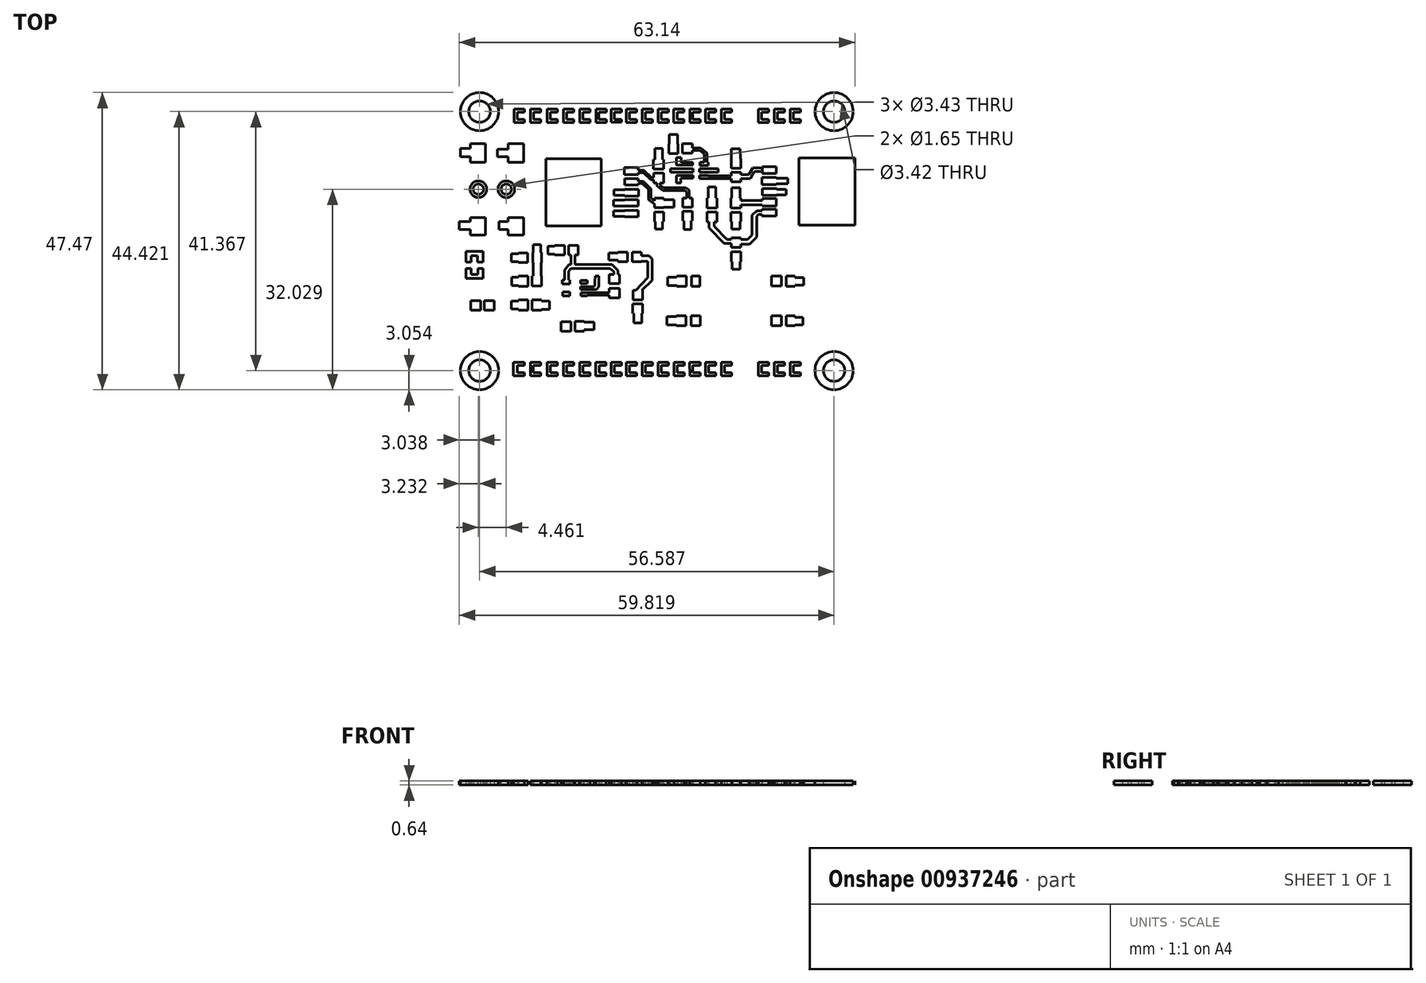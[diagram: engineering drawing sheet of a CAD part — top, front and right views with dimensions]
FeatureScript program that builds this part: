
annotation { "Feature Type Name" : "Feature", "Feature Type Description" : "" }
export const myFeature = defineFeature(function(context is Context, id is Id, definition is map)
    precondition{}
    {
        {
            var Q0;
            Q0=qCreatedBy(makeId("Top.planeOp"),FACE);
            var sketch = newSketch(context, id + "F0", { "sketchPlane" : qUnion([Q0])});
            skLineSegment(sketch, "E0.bottom", {"start": v(-31.07, 17.75) * mm, "end": v(37.51, 17.75) * mm});
            skLineSegment(sketch, "E0.top", {"start": v(-31.07, -35.59) * mm, "end": v(37.51, -35.59) * mm});
            skLineSegment(sketch, "E0.left", {"start": v(-31.07, 17.75) * mm, "end": v(-31.07, -35.59) * mm});
            skLineSegment(sketch, "E0.right", {"start": v(37.51, 17.75) * mm, "end": v(37.51, -35.59) * mm});
            skLineSegment(sketch, "E1.bottom", {"start": v(-26.63, 6.76) * mm, "end": v(-24.16, 6.76) * mm});
            skLineSegment(sketch, "E1.top", {"start": v(-26.63, 3.78) * mm, "end": v(-24.16, 3.78) * mm});
            skLineSegment(sketch, "E1.left", {"start": v(-26.63, 6.76) * mm, "end": v(-26.63, 3.78) * mm});
            skLineSegment(sketch, "E1.right", {"start": v(-24.16, 6.76) * mm, "end": v(-24.16, 3.78) * mm});
            skLineSegment(sketch, "E2.bottom", {"start": v(-20.57, 6.76) * mm, "end": v(-18.08, 6.76) * mm});
            skLineSegment(sketch, "E2.top", {"start": v(-20.57, 3.78) * mm, "end": v(-18.08, 3.78) * mm});
            skLineSegment(sketch, "E2.left", {"start": v(-20.57, 6.76) * mm, "end": v(-20.57, 3.78) * mm});
            skLineSegment(sketch, "E2.right", {"start": v(-18.08, 6.76) * mm, "end": v(-18.08, 3.78) * mm});
            skLineSegment(sketch, "E3.bottom", {"start": v(-26.63, -5.07) * mm, "end": v(-24.16, -5.07) * mm});
            skLineSegment(sketch, "E3.top", {"start": v(-26.63, -7.89) * mm, "end": v(-24.16, -7.89) * mm});
            skLineSegment(sketch, "E3.left", {"start": v(-26.63, -5.07) * mm, "end": v(-26.63, -7.89) * mm});
            skLineSegment(sketch, "E3.right", {"start": v(-24.16, -5.07) * mm, "end": v(-24.16, -7.89) * mm});
            skLineSegment(sketch, "E4.bottom", {"start": v(-20.57, -5.05) * mm, "end": v(-18.1, -5.05) * mm});
            skLineSegment(sketch, "E4.top", {"start": v(-20.57, -7.89) * mm, "end": v(-18.1, -7.89) * mm});
            skLineSegment(sketch, "E4.left", {"start": v(-20.57, -5.05) * mm, "end": v(-20.57, -7.89) * mm});
            skLineSegment(sketch, "E4.right", {"start": v(-18.1, -5.05) * mm, "end": v(-18.1, -7.89) * mm});
            skLineSegment(sketch, "E5.bottom", {"start": v(-26.53, -18.31) * mm, "end": v(-24.97, -18.31) * mm});
            skLineSegment(sketch, "E5.top", {"start": v(-26.53, -19.88) * mm, "end": v(-24.97, -19.88) * mm});
            skLineSegment(sketch, "E5.left", {"start": v(-26.53, -18.31) * mm, "end": v(-26.53, -19.88) * mm});
            skLineSegment(sketch, "E5.right", {"start": v(-24.97, -18.31) * mm, "end": v(-24.97, -19.88) * mm});
            skLineSegment(sketch, "E6.bottom", {"start": v(-24.36, -18.31) * mm, "end": v(-22.8, -18.31) * mm});
            skLineSegment(sketch, "E6.top", {"start": v(-24.36, -19.88) * mm, "end": v(-22.8, -19.88) * mm});
            skLineSegment(sketch, "E6.left", {"start": v(-24.36, -18.31) * mm, "end": v(-24.36, -19.88) * mm});
            skLineSegment(sketch, "E6.right", {"start": v(-22.8, -18.31) * mm, "end": v(-22.8, -19.88) * mm});
            skLineSegment(sketch, "E7.bottom", {"start": v(-18.92, -18.23) * mm, "end": v(-17.4, -18.23) * mm});
            skLineSegment(sketch, "E7.top", {"start": v(-18.92, -19.88) * mm, "end": v(-17.4, -19.88) * mm});
            skLineSegment(sketch, "E7.left", {"start": v(-18.92, -18.23) * mm, "end": v(-18.92, -19.88) * mm});
            skLineSegment(sketch, "E7.right", {"start": v(-17.4, -18.23) * mm, "end": v(-17.4, -19.88) * mm});
            skLineSegment(sketch, "E8.bottom", {"start": v(-16.76, -18.22) * mm, "end": v(-15.23, -18.22) * mm});
            skLineSegment(sketch, "E8.top", {"start": v(-16.76, -19.88) * mm, "end": v(-15.23, -19.88) * mm});
            skLineSegment(sketch, "E8.left", {"start": v(-16.76, -18.22) * mm, "end": v(-16.76, -19.88) * mm});
            skLineSegment(sketch, "E8.right", {"start": v(-15.23, -18.22) * mm, "end": v(-15.23, -19.88) * mm});
            skLineSegment(sketch, "E9.bottom", {"start": v(-18.95, -14.37) * mm, "end": v(-17.42, -14.37) * mm});
            skLineSegment(sketch, "E9.top", {"start": v(-18.95, -16.02) * mm, "end": v(-17.42, -16.02) * mm});
            skLineSegment(sketch, "E9.left", {"start": v(-18.95, -14.37) * mm, "end": v(-18.95, -16.02) * mm});
            skLineSegment(sketch, "E9.right", {"start": v(-17.42, -14.37) * mm, "end": v(-17.42, -16.02) * mm});
            skLineSegment(sketch, "E10.bottom", {"start": v(-16.76, -14.4) * mm, "end": v(-15.22, -14.4) * mm});
            skLineSegment(sketch, "E10.top", {"start": v(-16.76, -15.97) * mm, "end": v(-15.22, -15.97) * mm});
            skLineSegment(sketch, "E10.left", {"start": v(-16.76, -14.4) * mm, "end": v(-16.76, -15.97) * mm});
            skLineSegment(sketch, "E10.right", {"start": v(-15.22, -14.4) * mm, "end": v(-15.22, -15.97) * mm});
            skLineSegment(sketch, "E11.bottom", {"start": v(-18.92, -10.7) * mm, "end": v(-17.45, -10.7) * mm});
            skLineSegment(sketch, "E11.top", {"start": v(-18.92, -12.22) * mm, "end": v(-17.45, -12.22) * mm});
            skLineSegment(sketch, "E11.left", {"start": v(-18.92, -10.7) * mm, "end": v(-18.92, -12.22) * mm});
            skLineSegment(sketch, "E11.right", {"start": v(-17.45, -10.7) * mm, "end": v(-17.45, -12.22) * mm});
            skLineSegment(sketch, "E12.bottom", {"start": v(-16.66, -10.66) * mm, "end": v(-15.22, -10.66) * mm});
            skLineSegment(sketch, "E12.top", {"start": v(-16.66, -12.26) * mm, "end": v(-15.22, -12.26) * mm});
            skLineSegment(sketch, "E12.left", {"start": v(-16.66, -10.66) * mm, "end": v(-16.66, -12.26) * mm});
            skLineSegment(sketch, "E12.right", {"start": v(-15.22, -10.66) * mm, "end": v(-15.22, -12.26) * mm});
            skLineSegment(sketch, "E13.bottom", {"start": v(-13.14, -9.5) * mm, "end": v(-11.55, -9.5) * mm});
            skLineSegment(sketch, "E13.top", {"start": v(-13.14, -11.04) * mm, "end": v(-11.55, -11.04) * mm});
            skLineSegment(sketch, "E13.left", {"start": v(-13.14, -9.5) * mm, "end": v(-13.14, -11.04) * mm});
            skLineSegment(sketch, "E13.right", {"start": v(-11.55, -9.5) * mm, "end": v(-11.55, -11.04) * mm});
            skLineSegment(sketch, "E14.bottom", {"start": v(-10.92, -9.52) * mm, "end": v(-9.4, -9.52) * mm});
            skLineSegment(sketch, "E14.top", {"start": v(-10.92, -11.03) * mm, "end": v(-9.4, -11.03) * mm});
            skLineSegment(sketch, "E14.left", {"start": v(-10.92, -9.52) * mm, "end": v(-10.92, -11.03) * mm});
            skLineSegment(sketch, "E14.right", {"start": v(-9.4, -9.52) * mm, "end": v(-9.4, -11.03) * mm});
            skLineSegment(sketch, "E15.bottom", {"start": v(-11.94, -15.04) * mm, "end": v(-10.75, -15.04) * mm});
            skLineSegment(sketch, "E15.top", {"start": v(-11.94, -15.65) * mm, "end": v(-10.75, -15.65) * mm});
            skLineSegment(sketch, "E15.left", {"start": v(-11.94, -15.04) * mm, "end": v(-11.94, -15.65) * mm});
            skLineSegment(sketch, "E15.right", {"start": v(-10.75, -15.04) * mm, "end": v(-10.75, -15.65) * mm});
            skLineSegment(sketch, "E16.bottom", {"start": v(-9.02, -15.07) * mm, "end": v(-7.94, -15.07) * mm});
            skLineSegment(sketch, "E16.top", {"start": v(-9.02, -15.58) * mm, "end": v(-7.94, -15.58) * mm});
            skLineSegment(sketch, "E16.left", {"start": v(-9.02, -15.07) * mm, "end": v(-9.02, -15.58) * mm});
            skLineSegment(sketch, "E16.right", {"start": v(-7.94, -15.07) * mm, "end": v(-7.94, -15.58) * mm});
            skLineSegment(sketch, "E17.bottom", {"start": v(-9.02, -16.11) * mm, "end": v(-7.94, -16.11) * mm});
            skLineSegment(sketch, "E17.top", {"start": v(-9.02, -16.57) * mm, "end": v(-7.94, -16.57) * mm});
            skLineSegment(sketch, "E17.left", {"start": v(-9.02, -16.11) * mm, "end": v(-9.02, -16.57) * mm});
            skLineSegment(sketch, "E17.right", {"start": v(-7.94, -16.11) * mm, "end": v(-7.94, -16.57) * mm});
            skLineSegment(sketch, "E18.bottom", {"start": v(-8.98, -17.09) * mm, "end": v(-7.92, -17.09) * mm});
            skLineSegment(sketch, "E18.top", {"start": v(-8.98, -17.56) * mm, "end": v(-7.92, -17.56) * mm});
            skLineSegment(sketch, "E18.left", {"start": v(-8.98, -17.09) * mm, "end": v(-8.98, -17.56) * mm});
            skLineSegment(sketch, "E18.right", {"start": v(-7.92, -17.09) * mm, "end": v(-7.92, -17.56) * mm});
            skLineSegment(sketch, "E19.bottom", {"start": v(-11.85, -16.92) * mm, "end": v(-10.75, -16.92) * mm});
            skLineSegment(sketch, "E19.top", {"start": v(-11.85, -17.55) * mm, "end": v(-10.75, -17.55) * mm});
            skLineSegment(sketch, "E19.left", {"start": v(-11.85, -16.92) * mm, "end": v(-11.85, -17.55) * mm});
            skLineSegment(sketch, "E19.right", {"start": v(-10.75, -16.92) * mm, "end": v(-10.75, -17.55) * mm});
            skLineSegment(sketch, "E20.bottom", {"start": v(-4.44, -14.17) * mm, "end": v(-2.8, -14.17) * mm});
            skLineSegment(sketch, "E20.top", {"start": v(-4.44, -15.62) * mm, "end": v(-2.8, -15.62) * mm});
            skLineSegment(sketch, "E20.left", {"start": v(-4.44, -14.17) * mm, "end": v(-4.44, -15.62) * mm});
            skLineSegment(sketch, "E20.right", {"start": v(-2.8, -14.17) * mm, "end": v(-2.8, -15.62) * mm});
            skLineSegment(sketch, "E21.bottom", {"start": v(-4.43, -16.34) * mm, "end": v(-2.81, -16.34) * mm});
            skLineSegment(sketch, "E21.top", {"start": v(-4.43, -17.87) * mm, "end": v(-2.81, -17.87) * mm});
            skLineSegment(sketch, "E21.left", {"start": v(-4.43, -16.34) * mm, "end": v(-4.43, -17.87) * mm});
            skLineSegment(sketch, "E21.right", {"start": v(-2.81, -16.34) * mm, "end": v(-2.81, -17.87) * mm});
            skLineSegment(sketch, "E22.bottom", {"start": v(-12.1, -21.7) * mm, "end": v(-10.55, -21.7) * mm});
            skLineSegment(sketch, "E22.top", {"start": v(-12.1, -23.23) * mm, "end": v(-10.55, -23.23) * mm});
            skLineSegment(sketch, "E22.left", {"start": v(-12.1, -21.7) * mm, "end": v(-12.1, -23.23) * mm});
            skLineSegment(sketch, "E22.right", {"start": v(-10.55, -21.7) * mm, "end": v(-10.55, -23.23) * mm});
            skLineSegment(sketch, "E23.bottom", {"start": v(-9.93, -21.66) * mm, "end": v(-8.43, -21.66) * mm});
            skLineSegment(sketch, "E23.top", {"start": v(-9.93, -23.22) * mm, "end": v(-8.43, -23.22) * mm});
            skLineSegment(sketch, "E23.left", {"start": v(-9.93, -21.66) * mm, "end": v(-9.93, -23.22) * mm});
            skLineSegment(sketch, "E23.right", {"start": v(-8.43, -21.66) * mm, "end": v(-8.43, -23.22) * mm});
            skLineSegment(sketch, "E24.bottom", {"start": v(-0.66, -16.68) * mm, "end": v(0.91, -16.68) * mm});
            skLineSegment(sketch, "E24.top", {"start": v(-0.66, -18.23) * mm, "end": v(0.91, -18.23) * mm});
            skLineSegment(sketch, "E24.left", {"start": v(-0.66, -16.68) * mm, "end": v(-0.66, -18.23) * mm});
            skLineSegment(sketch, "E24.right", {"start": v(0.91, -16.68) * mm, "end": v(0.91, -18.23) * mm});
            skLineSegment(sketch, "E25.bottom", {"start": v(-0.68, -18.86) * mm, "end": v(0.91, -18.86) * mm});
            skLineSegment(sketch, "E25.top", {"start": v(-0.68, -20.36) * mm, "end": v(0.91, -20.36) * mm});
            skLineSegment(sketch, "E25.left", {"start": v(-0.68, -18.86) * mm, "end": v(-0.68, -20.36) * mm});
            skLineSegment(sketch, "E25.right", {"start": v(0.91, -18.86) * mm, "end": v(0.91, -20.36) * mm});
            skLineSegment(sketch, "E26.bottom", {"start": v(-3.03, -10.56) * mm, "end": v(-1.5, -10.56) * mm});
            skLineSegment(sketch, "E26.top", {"start": v(-3.03, -12.08) * mm, "end": v(-1.5, -12.08) * mm});
            skLineSegment(sketch, "E26.left", {"start": v(-3.03, -10.56) * mm, "end": v(-3.03, -12.08) * mm});
            skLineSegment(sketch, "E26.right", {"start": v(-1.5, -10.56) * mm, "end": v(-1.5, -12.08) * mm});
            skLineSegment(sketch, "E27.bottom", {"start": v(-0.78, -10.56) * mm, "end": v(0.7, -10.56) * mm});
            skLineSegment(sketch, "E27.top", {"start": v(-0.78, -12.1) * mm, "end": v(0.7, -12.1) * mm});
            skLineSegment(sketch, "E27.left", {"start": v(-0.78, -10.56) * mm, "end": v(-0.78, -12.1) * mm});
            skLineSegment(sketch, "E27.right", {"start": v(0.7, -10.56) * mm, "end": v(0.7, -12.1) * mm});
            skLineSegment(sketch, "E28.bottom", {"start": v(6.35, -14.4) * mm, "end": v(7.85, -14.4) * mm});
            skLineSegment(sketch, "E28.top", {"start": v(6.35, -16.02) * mm, "end": v(7.85, -16.02) * mm});
            skLineSegment(sketch, "E28.left", {"start": v(6.35, -14.4) * mm, "end": v(6.35, -16.02) * mm});
            skLineSegment(sketch, "E28.right", {"start": v(7.85, -14.4) * mm, "end": v(7.85, -16.02) * mm});
            skLineSegment(sketch, "E29.bottom", {"start": v(8.67, -14.4) * mm, "end": v(10.04, -14.4) * mm});
            skLineSegment(sketch, "E29.top", {"start": v(8.67, -16.04) * mm, "end": v(10.04, -16.04) * mm});
            skLineSegment(sketch, "E29.left", {"start": v(8.67, -14.4) * mm, "end": v(8.67, -16.04) * mm});
            skLineSegment(sketch, "E29.right", {"start": v(10.04, -14.4) * mm, "end": v(10.04, -16.04) * mm});
            skLineSegment(sketch, "E30.bottom", {"start": v(6.3, -20.72) * mm, "end": v(7.84, -20.72) * mm});
            skLineSegment(sketch, "E30.top", {"start": v(6.3, -22.36) * mm, "end": v(7.84, -22.36) * mm});
            skLineSegment(sketch, "E30.left", {"start": v(6.3, -20.72) * mm, "end": v(6.3, -22.36) * mm});
            skLineSegment(sketch, "E30.right", {"start": v(7.84, -20.72) * mm, "end": v(7.84, -22.36) * mm});
            skLineSegment(sketch, "E31.bottom", {"start": v(8.65, -20.75) * mm, "end": v(10.09, -20.75) * mm});
            skLineSegment(sketch, "E31.top", {"start": v(8.65, -22.33) * mm, "end": v(10.09, -22.33) * mm});
            skLineSegment(sketch, "E31.left", {"start": v(8.65, -20.75) * mm, "end": v(8.65, -22.33) * mm});
            skLineSegment(sketch, "E31.right", {"start": v(10.09, -20.75) * mm, "end": v(10.09, -22.33) * mm});
            skLineSegment(sketch, "E32.bottom", {"start": v(21.47, -20.74) * mm, "end": v(23.04, -20.74) * mm});
            skLineSegment(sketch, "E32.top", {"start": v(21.47, -22.34) * mm, "end": v(23.04, -22.34) * mm});
            skLineSegment(sketch, "E32.left", {"start": v(21.47, -20.74) * mm, "end": v(21.47, -22.34) * mm});
            skLineSegment(sketch, "E32.right", {"start": v(23.04, -20.74) * mm, "end": v(23.04, -22.34) * mm});
            skLineSegment(sketch, "E33.bottom", {"start": v(23.84, -20.72) * mm, "end": v(25.2, -20.72) * mm});
            skLineSegment(sketch, "E33.top", {"start": v(23.84, -22.35) * mm, "end": v(25.2, -22.35) * mm});
            skLineSegment(sketch, "E33.left", {"start": v(23.84, -20.72) * mm, "end": v(23.84, -22.35) * mm});
            skLineSegment(sketch, "E33.right", {"start": v(25.2, -20.72) * mm, "end": v(25.2, -22.35) * mm});
            skLineSegment(sketch, "E34.bottom", {"start": v(21.5, -14.4) * mm, "end": v(23.04, -14.4) * mm});
            skLineSegment(sketch, "E34.top", {"start": v(21.5, -16.01) * mm, "end": v(23.04, -16.01) * mm});
            skLineSegment(sketch, "E34.left", {"start": v(21.5, -14.4) * mm, "end": v(21.5, -16.01) * mm});
            skLineSegment(sketch, "E34.right", {"start": v(23.04, -14.4) * mm, "end": v(23.04, -16.01) * mm});
            skLineSegment(sketch, "E35.bottom", {"start": v(23.82, -14.4) * mm, "end": v(25.2, -14.4) * mm});
            skLineSegment(sketch, "E35.top", {"start": v(23.82, -16.05) * mm, "end": v(25.2, -16.05) * mm});
            skLineSegment(sketch, "E35.left", {"start": v(23.82, -14.4) * mm, "end": v(23.82, -16.05) * mm});
            skLineSegment(sketch, "E35.right", {"start": v(25.2, -14.4) * mm, "end": v(25.2, -16.05) * mm});
            skLineSegment(sketch, "E36.bottom", {"start": v(15.02, -8.31) * mm, "end": v(16.56, -8.31) * mm});
            skLineSegment(sketch, "E36.top", {"start": v(15.02, -9.8) * mm, "end": v(16.56, -9.8) * mm});
            skLineSegment(sketch, "E36.left", {"start": v(15.02, -8.31) * mm, "end": v(15.02, -9.8) * mm});
            skLineSegment(sketch, "E36.right", {"start": v(16.56, -8.31) * mm, "end": v(16.56, -9.8) * mm});
            skLineSegment(sketch, "E37.bottom", {"start": v(15.02, -10.53) * mm, "end": v(16.56, -10.53) * mm});
            skLineSegment(sketch, "E37.top", {"start": v(15.02, -12.1) * mm, "end": v(16.56, -12.1) * mm});
            skLineSegment(sketch, "E37.left", {"start": v(15.02, -10.53) * mm, "end": v(15.02, -12.1) * mm});
            skLineSegment(sketch, "E37.right", {"start": v(16.56, -10.53) * mm, "end": v(16.56, -12.1) * mm});
            skLineSegment(sketch, "E38.bottom", {"start": v(-14.57, 4.35) * mm, "end": v(-5.73, 4.35) * mm});
            skLineSegment(sketch, "E38.top", {"start": v(-14.57, -6.38) * mm, "end": v(-5.73, -6.38) * mm});
            skLineSegment(sketch, "E38.left", {"start": v(-14.57, 4.35) * mm, "end": v(-14.57, -6.38) * mm});
            skLineSegment(sketch, "E38.right", {"start": v(-5.73, 4.35) * mm, "end": v(-5.73, -6.38) * mm});
            skLineSegment(sketch, "E39.bottom", {"start": v(-2.05, 2.91) * mm, "end": v(0.22, 2.91) * mm});
            skLineSegment(sketch, "E39.top", {"start": v(-2.05, 1.8) * mm, "end": v(0.22, 1.8) * mm});
            skLineSegment(sketch, "E39.left", {"start": v(-2.05, 2.91) * mm, "end": v(-2.05, 1.8) * mm});
            skLineSegment(sketch, "E39.right", {"start": v(0.22, 2.91) * mm, "end": v(0.22, 1.8) * mm});
            skLineSegment(sketch, "E40.bottom", {"start": v(-1.99, 1.18) * mm, "end": v(0.2, 1.18) * mm});
            skLineSegment(sketch, "E40.top", {"start": v(-1.99, 0.15) * mm, "end": v(0.2, 0.15) * mm});
            skLineSegment(sketch, "E40.left", {"start": v(-1.99, 1.18) * mm, "end": v(-1.99, 0.15) * mm});
            skLineSegment(sketch, "E41.bottom", {"start": v(-1.96, -0.53) * mm, "end": v(0.24, -0.53) * mm});
            skLineSegment(sketch, "E41.top", {"start": v(-1.96, -1.6) * mm, "end": v(0.24, -1.6) * mm});
            skLineSegment(sketch, "E41.left", {"start": v(-1.96, -0.53) * mm, "end": v(-1.96, -1.6) * mm});
            skLineSegment(sketch, "E41.right", {"start": v(0.24, -0.53) * mm, "end": v(0.24, -1.6) * mm});
            skLineSegment(sketch, "E42.bottom", {"start": v(-1.96, -2.2) * mm, "end": v(0.2, -2.2) * mm});
            skLineSegment(sketch, "E42.top", {"start": v(-1.96, -3.25) * mm, "end": v(0.2, -3.25) * mm});
            skLineSegment(sketch, "E42.left", {"start": v(-1.96, -2.2) * mm, "end": v(-1.96, -3.25) * mm});
            skLineSegment(sketch, "E42.right", {"start": v(0.2, -2.2) * mm, "end": v(0.2, -3.25) * mm});
            skLineSegment(sketch, "E43.bottom", {"start": v(-1.94, -3.92) * mm, "end": v(0.2, -3.92) * mm});
            skLineSegment(sketch, "E43.top", {"start": v(-1.94, -4.94) * mm, "end": v(0.2, -4.94) * mm});
            skLineSegment(sketch, "E43.left", {"start": v(-1.94, -3.92) * mm, "end": v(-1.94, -4.94) * mm});
            skLineSegment(sketch, "E43.right", {"start": v(0.2, -3.92) * mm, "end": v(0.2, -4.94) * mm});
            skLineSegment(sketch, "E44.bottom", {"start": v(2.78, -1.98) * mm, "end": v(4.26, -1.98) * mm});
            skLineSegment(sketch, "E44.top", {"start": v(2.78, -3.48) * mm, "end": v(4.26, -3.48) * mm});
            skLineSegment(sketch, "E45.bottom", {"start": v(2.78, -4.17) * mm, "end": v(4.26, -4.17) * mm});
            skLineSegment(sketch, "E45.top", {"start": v(2.78, -5.72) * mm, "end": v(4.26, -5.72) * mm});
            skLineSegment(sketch, "E45.left", {"start": v(2.78, -4.17) * mm, "end": v(2.78, -5.72) * mm});
            skLineSegment(sketch, "E45.right", {"start": v(4.26, -4.17) * mm, "end": v(4.26, -5.72) * mm});
            skLineSegment(sketch, "E46.bottom", {"start": v(7.3, -1.98) * mm, "end": v(8.83, -1.98) * mm});
            skLineSegment(sketch, "E46.top", {"start": v(7.3, -3.38) * mm, "end": v(8.83, -3.38) * mm});
            skLineSegment(sketch, "E46.left", {"start": v(7.3, -1.98) * mm, "end": v(7.3, -3.38) * mm});
            skLineSegment(sketch, "E46.right", {"start": v(8.83, -1.98) * mm, "end": v(8.83, -3.38) * mm});
            skLineSegment(sketch, "E47.bottom", {"start": v(7.33, -4.04) * mm, "end": v(8.8, -4.04) * mm});
            skLineSegment(sketch, "E47.top", {"start": v(7.33, -5.56) * mm, "end": v(8.8, -5.56) * mm});
            skLineSegment(sketch, "E47.left", {"start": v(7.33, -4.04) * mm, "end": v(7.33, -5.56) * mm});
            skLineSegment(sketch, "E47.right", {"start": v(8.8, -4.04) * mm, "end": v(8.8, -5.56) * mm});
            skLineSegment(sketch, "E48.bottom", {"start": v(11.2, -1.98) * mm, "end": v(12.75, -1.98) * mm});
            skLineSegment(sketch, "E48.top", {"start": v(11.2, -3.53) * mm, "end": v(12.75, -3.53) * mm});
            skLineSegment(sketch, "E48.left", {"start": v(11.2, -1.98) * mm, "end": v(11.2, -3.53) * mm});
            skLineSegment(sketch, "E48.right", {"start": v(12.75, -1.98) * mm, "end": v(12.75, -3.53) * mm});
            skLineSegment(sketch, "E49.bottom", {"start": v(11.18, -4.2) * mm, "end": v(12.8, -4.2) * mm});
            skLineSegment(sketch, "E49.top", {"start": v(11.18, -5.74) * mm, "end": v(12.8, -5.74) * mm});
            skLineSegment(sketch, "E49.left", {"start": v(11.18, -4.2) * mm, "end": v(11.18, -5.74) * mm});
            skLineSegment(sketch, "E49.right", {"start": v(12.8, -4.2) * mm, "end": v(12.8, -5.74) * mm});
            skLineSegment(sketch, "E50.bottom", {"start": v(15, -1.98) * mm, "end": v(16.56, -1.98) * mm});
            skLineSegment(sketch, "E50.top", {"start": v(15, -3.53) * mm, "end": v(16.56, -3.53) * mm});
            skLineSegment(sketch, "E50.left", {"start": v(15, -1.98) * mm, "end": v(15, -3.53) * mm});
            skLineSegment(sketch, "E50.right", {"start": v(16.56, -1.98) * mm, "end": v(16.56, -3.53) * mm});
            skLineSegment(sketch, "E51.bottom", {"start": v(15, -4.21) * mm, "end": v(16.56, -4.21) * mm});
            skLineSegment(sketch, "E51.top", {"start": v(15, -5.7) * mm, "end": v(16.56, -5.7) * mm});
            skLineSegment(sketch, "E51.left", {"start": v(15, -4.21) * mm, "end": v(15, -5.7) * mm});
            skLineSegment(sketch, "E51.right", {"start": v(16.56, -4.21) * mm, "end": v(16.56, -5.7) * mm});
            skLineSegment(sketch, "E52.bottom", {"start": v(2.63, 4.23) * mm, "end": v(4.26, 4.23) * mm});
            skLineSegment(sketch, "E52.top", {"start": v(2.63, 2.69) * mm, "end": v(4.26, 2.69) * mm});
            skLineSegment(sketch, "E52.left", {"start": v(2.63, 4.23) * mm, "end": v(2.63, 2.69) * mm});
            skLineSegment(sketch, "E52.right", {"start": v(4.26, 4.23) * mm, "end": v(4.26, 2.69) * mm});
            skLineSegment(sketch, "E53.bottom", {"start": v(2.69, 2.05) * mm, "end": v(4.26, 2.05) * mm});
            skLineSegment(sketch, "E53.top", {"start": v(2.69, 0.47) * mm, "end": v(4.26, 0.47) * mm});
            skLineSegment(sketch, "E53.left", {"start": v(2.69, 2.05) * mm, "end": v(2.69, 0.47) * mm});
            skLineSegment(sketch, "E53.right", {"start": v(4.26, 2.05) * mm, "end": v(4.26, 0.47) * mm});
            skLineSegment(sketch, "E54.bottom", {"start": v(5.07, 6.7) * mm, "end": v(6.56, 6.7) * mm});
            skLineSegment(sketch, "E54.top", {"start": v(5.07, 5.16) * mm, "end": v(6.56, 5.16) * mm});
            skLineSegment(sketch, "E54.left", {"start": v(5.07, 6.7) * mm, "end": v(5.07, 5.16) * mm});
            skLineSegment(sketch, "E54.right", {"start": v(6.56, 6.7) * mm, "end": v(6.56, 5.16) * mm});
            skLineSegment(sketch, "E55.bottom", {"start": v(7.25, 6.75) * mm, "end": v(8.8, 6.75) * mm});
            skLineSegment(sketch, "E55.top", {"start": v(7.25, 5.2) * mm, "end": v(8.8, 5.2) * mm});
            skLineSegment(sketch, "E55.left", {"start": v(7.25, 6.75) * mm, "end": v(7.25, 5.2) * mm});
            skLineSegment(sketch, "E55.right", {"start": v(8.8, 6.75) * mm, "end": v(8.8, 5.2) * mm});
            skLineSegment(sketch, "E56.bottom", {"start": v(7.57, 3.78) * mm, "end": v(8.91, 3.78) * mm});
            skLineSegment(sketch, "E56.top", {"start": v(7.57, 3.34) * mm, "end": v(8.91, 3.34) * mm});
            skLineSegment(sketch, "E56.left", {"start": v(7.57, 3.78) * mm, "end": v(7.57, 3.34) * mm});
            skLineSegment(sketch, "E56.right", {"start": v(8.91, 3.78) * mm, "end": v(8.91, 3.34) * mm});
            skLineSegment(sketch, "E57.bottom", {"start": v(7.65, 2.78) * mm, "end": v(8.93, 2.78) * mm});
            skLineSegment(sketch, "E57.top", {"start": v(7.65, 2.18) * mm, "end": v(8.93, 2.18) * mm});
            skLineSegment(sketch, "E57.left", {"start": v(7.65, 2.78) * mm, "end": v(7.65, 2.18) * mm});
            skLineSegment(sketch, "E57.right", {"start": v(8.93, 2.78) * mm, "end": v(8.93, 2.18) * mm});
            skLineSegment(sketch, "E58.bottom", {"start": v(7.56, 1.64) * mm, "end": v(8.93, 1.64) * mm});
            skLineSegment(sketch, "E58.top", {"start": v(7.56, 1.2) * mm, "end": v(8.93, 1.2) * mm});
            skLineSegment(sketch, "E58.left", {"start": v(7.56, 1.64) * mm, "end": v(7.56, 1.2) * mm});
            skLineSegment(sketch, "E58.right", {"start": v(8.93, 1.64) * mm, "end": v(8.93, 1.2) * mm});
            skLineSegment(sketch, "E59.bottom", {"start": v(10.04, 3.78) * mm, "end": v(11.4, 3.78) * mm});
            skLineSegment(sketch, "E59.top", {"start": v(10.04, 3.28) * mm, "end": v(11.4, 3.28) * mm});
            skLineSegment(sketch, "E59.left", {"start": v(10.04, 3.78) * mm, "end": v(10.04, 3.28) * mm});
            skLineSegment(sketch, "E59.right", {"start": v(11.4, 3.78) * mm, "end": v(11.4, 3.28) * mm});
            skLineSegment(sketch, "E60.bottom", {"start": v(10, 2.76) * mm, "end": v(11.41, 2.76) * mm});
            skLineSegment(sketch, "E60.top", {"start": v(10, 2.2) * mm, "end": v(11.41, 2.2) * mm});
            skLineSegment(sketch, "E60.left", {"start": v(10, 2.76) * mm, "end": v(10, 2.2) * mm});
            skLineSegment(sketch, "E60.right", {"start": v(11.41, 2.76) * mm, "end": v(11.41, 2.2) * mm});
            skLineSegment(sketch, "E61.bottom", {"start": v(10, 1.64) * mm, "end": v(11.38, 1.64) * mm});
            skLineSegment(sketch, "E61.top", {"start": v(10, 1.19) * mm, "end": v(11.38, 1.19) * mm});
            skLineSegment(sketch, "E61.left", {"start": v(10, 1.64) * mm, "end": v(10, 1.19) * mm});
            skLineSegment(sketch, "E61.right", {"start": v(11.38, 1.64) * mm, "end": v(11.38, 1.19) * mm});
            skLineSegment(sketch, "E62.bottom", {"start": v(15.05, 4.36) * mm, "end": v(16.57, 4.36) * mm});
            skLineSegment(sketch, "E62.top", {"start": v(15.05, 2.82) * mm, "end": v(16.57, 2.82) * mm});
            skLineSegment(sketch, "E62.left", {"start": v(15.05, 4.36) * mm, "end": v(15.05, 2.82) * mm});
            skLineSegment(sketch, "E62.right", {"start": v(16.57, 4.36) * mm, "end": v(16.57, 2.82) * mm});
            skLineSegment(sketch, "E63.bottom", {"start": v(15.05, 2.15) * mm, "end": v(16.57, 2.15) * mm});
            skLineSegment(sketch, "E63.top", {"start": v(15.05, 0.63) * mm, "end": v(16.57, 0.63) * mm});
            skLineSegment(sketch, "E63.left", {"start": v(15.05, 2.15) * mm, "end": v(15.05, 0.63) * mm});
            skLineSegment(sketch, "E63.right", {"start": v(16.57, 2.15) * mm, "end": v(16.57, 0.63) * mm});
            skLineSegment(sketch, "E64.bottom", {"start": v(19.98, 3.05) * mm, "end": v(22.23, 3.05) * mm});
            skLineSegment(sketch, "E64.top", {"start": v(19.98, 1.97) * mm, "end": v(22.23, 1.97) * mm});
            skLineSegment(sketch, "E64.left", {"start": v(19.98, 3.05) * mm, "end": v(19.98, 1.97) * mm});
            skLineSegment(sketch, "E64.right", {"start": v(22.23, 3.05) * mm, "end": v(22.23, 1.97) * mm});
            skLineSegment(sketch, "E65.bottom", {"start": v(19.93, 1.34) * mm, "end": v(22.23, 1.34) * mm});
            skLineSegment(sketch, "E65.top", {"start": v(19.93, 0.24) * mm, "end": v(22.23, 0.24) * mm});
            skLineSegment(sketch, "E65.left", {"start": v(19.93, 1.34) * mm, "end": v(19.93, 0.24) * mm});
            skLineSegment(sketch, "E65.right", {"start": v(22.23, 1.34) * mm, "end": v(22.23, 0.24) * mm});
            skLineSegment(sketch, "E66.bottom", {"start": v(19.98, -0.45) * mm, "end": v(22.27, -0.45) * mm});
            skLineSegment(sketch, "E66.top", {"start": v(19.98, -1.5) * mm, "end": v(22.27, -1.5) * mm});
            skLineSegment(sketch, "E66.left", {"start": v(19.98, -0.45) * mm, "end": v(19.98, -1.5) * mm});
            skLineSegment(sketch, "E66.right", {"start": v(22.27, -0.45) * mm, "end": v(22.27, -1.5) * mm});
            skLineSegment(sketch, "E67.bottom", {"start": v(19.98, -2.02) * mm, "end": v(22.22, -2.02) * mm});
            skLineSegment(sketch, "E67.top", {"start": v(19.98, -3.2) * mm, "end": v(22.22, -3.2) * mm});
            skLineSegment(sketch, "E67.left", {"start": v(19.98, -2.02) * mm, "end": v(19.98, -3.2) * mm});
            skLineSegment(sketch, "E67.right", {"start": v(22.22, -2.02) * mm, "end": v(22.22, -3.2) * mm});
            skLineSegment(sketch, "E68.bottom", {"start": v(19.96, -3.75) * mm, "end": v(22.22, -3.75) * mm});
            skLineSegment(sketch, "E68.top", {"start": v(19.96, -4.82) * mm, "end": v(22.22, -4.82) * mm});
            skLineSegment(sketch, "E68.left", {"start": v(19.96, -3.75) * mm, "end": v(19.96, -4.82) * mm});
            skLineSegment(sketch, "E68.right", {"start": v(22.22, -3.75) * mm, "end": v(22.22, -4.82) * mm});
            skLineSegment(sketch, "E69.bottom", {"start": v(25.83, 4.45) * mm, "end": v(34.78, 4.45) * mm});
            skLineSegment(sketch, "E69.top", {"start": v(25.83, -6.28) * mm, "end": v(34.78, -6.28) * mm});
            skLineSegment(sketch, "E69.left", {"start": v(25.83, 4.45) * mm, "end": v(25.83, -6.28) * mm});
            skLineSegment(sketch, "E69.right", {"start": v(34.78, 4.45) * mm, "end": v(34.78, -6.28) * mm});
            skPoint(sketch, "E70.centerSnap0", {"position": v(-16.66, -11.46) * mm});
            skPoint(sketch, "E71.centerSnap0", {"position": v(-8.48, -15.07) * mm});
            skPoint(sketch, "E72.centerSnap0", {"position": v(15.78, -5.7) * mm});
            skLineSegment(sketch, "E73", {"start": v(-11.33, -17.55) * mm, "end": v(-10.99, -17.55) * mm});
            skLineSegment(sketch, "E74", {"start": v(-10.99, -17.55) * mm, "end": v(-10.99, -21.7) * mm});
            skLineSegment(sketch, "E75", {"start": v(-10.99, -21.7) * mm, "end": v(-11.33, -21.7) * mm});
            skLineSegment(sketch, "E76", {"start": v(-11.57, -13.42) * mm, "end": v(-10.85, -12.55) * mm});
            skLineSegment(sketch, "E77", {"start": v(-10.85, -12.55) * mm, "end": v(-10.56, -12.55) * mm});
            skLineSegment(sketch, "E78", {"start": v(-10.56, -12.55) * mm, "end": v(-10.56, -11.03) * mm});
            skLineSegment(sketch, "E79", {"start": v(-10.56, -11.03) * mm, "end": v(-9.88, -11.03) * mm});
            skLineSegment(sketch, "E80", {"start": v(-9.88, -11.03) * mm, "end": v(-9.88, -12.53) * mm});
            skLineSegment(sketch, "E81", {"start": v(-9.88, -12.53) * mm, "end": v(-4, -12.53) * mm});
            skLineSegment(sketch, "E82", {"start": v(-4, -12.53) * mm, "end": v(-3.05, -13.5) * mm});
            skLineSegment(sketch, "E83", {"start": v(-3.05, -13.5) * mm, "end": v(-3.05, -14.17) * mm});
            skLineSegment(sketch, "E84", {"start": v(-3.05, -14.17) * mm, "end": v(-3.62, -14.17) * mm});
            skLineSegment(sketch, "E85", {"start": v(-3.7, -14.17) * mm, "end": v(-3.7, -13.73) * mm});
            skLineSegment(sketch, "E86", {"start": v(-3.7, -13.73) * mm, "end": v(-4.3, -13.18) * mm});
            skLineSegment(sketch, "E87", {"start": v(-4.3, -13.18) * mm, "end": v(-10.53, -13.18) * mm});
            skLineSegment(sketch, "E88", {"start": v(-10.53, -13.18) * mm, "end": v(-10.95, -13.63) * mm});
            skLineSegment(sketch, "E89", {"start": v(-10.95, -13.63) * mm, "end": v(-10.95, -15.04) * mm});
            skLineSegment(sketch, "E90", {"start": v(-10.95, -15.04) * mm, "end": v(-11.57, -15.04) * mm});
            skLineSegment(sketch, "E91", {"start": v(-8.85, -15.07) * mm, "end": v(-8.06, -15.07) * mm});
            skLineSegment(sketch, "E92", {"start": v(-7.94, -16.11) * mm, "end": v(-6.93, -16.11) * mm});
            skLineSegment(sketch, "E93", {"start": v(-6.93, -16.11) * mm, "end": v(-6.73, -15.92) * mm});
            skLineSegment(sketch, "E94", {"start": v(-6.73, -15.92) * mm, "end": v(-6.73, -15.36) * mm});
            skLineSegment(sketch, "E95", {"start": v(-6.12, -15.36) * mm, "end": v(-6.12, -16.14) * mm});
            skLineSegment(sketch, "E96", {"start": v(-6.12, -16.14) * mm, "end": v(-6.5, -16.57) * mm});
            skLineSegment(sketch, "E97", {"start": v(-7.92, -17.09) * mm, "end": v(-4.43, -17.08) * mm});
            skLineSegment(sketch, "E98", {"start": v(-4.43, -17.08) * mm, "end": v(-4.43, -17.41) * mm});
            skLineSegment(sketch, "E99", {"start": v(-4.43, -17.41) * mm, "end": v(-7.92, -17.41) * mm});
            skLineSegment(sketch, "E100", {"start": v(-7.92, -17.41) * mm, "end": v(-7.92, -17.09) * mm});
            skLineSegment(sketch, "E101", {"start": v(-8.43, -23.07) * mm, "end": v(-8.43, -21.78) * mm});
            skLineSegment(sketch, "E102", {"start": v(1.74, -14.64) * mm, "end": v(-0.2, -16.68) * mm});
            skLineSegment(sketch, "E103", {"start": v(-0.2, -16.68) * mm, "end": v(0.91, -16.68) * mm});
            skLineSegment(sketch, "E104", {"start": v(0.7, -11.17) * mm, "end": v(1.88, -11.17) * mm});
            skLineSegment(sketch, "E105", {"start": v(1.88, -11.17) * mm, "end": v(2.4, -11.65) * mm});
            skLineSegment(sketch, "E106", {"start": v(2.4, -11.65) * mm, "end": v(2.4, -15.11) * mm});
            skLineSegment(sketch, "E107", {"start": v(2.4, -15.11) * mm, "end": v(0.78, -16.68) * mm});
            skLineSegment(sketch, "E108", {"start": v(0.78, -16.68) * mm, "end": v(-0.2, -16.68) * mm});
            skLineSegment(sketch, "E109", {"start": v(21.5, -15.22) * mm, "end": v(21.5, -15.6) * mm});
            skLineSegment(sketch, "E110", {"start": v(21.5, -15.6) * mm, "end": v(10.04, -15.6) * mm});
            skLineSegment(sketch, "E111", {"start": v(21.47, -21.54) * mm, "end": v(21.47, -21.97) * mm});
            skLineSegment(sketch, "E112", {"start": v(21.47, -21.97) * mm, "end": v(10.09, -21.97) * mm});
            skLineSegment(sketch, "E113", {"start": v(10.09, -21.97) * mm, "end": v(10.09, -21.54) * mm});
            skLineSegment(sketch, "E114", {"start": v(-15.3, -12.26) * mm, "end": v(-15.3, -14.4) * mm});
            skLineSegment(sketch, "E115", {"start": v(-16.62, -12.26) * mm, "end": v(-15.3, -12.26) * mm});
            skLineSegment(sketch, "E116", {"start": v(11.48, -5.74) * mm, "end": v(11.48, -6.74) * mm});
            skLineSegment(sketch, "E117", {"start": v(11.48, -6.74) * mm, "end": v(13.89, -9.2) * mm});
            skLineSegment(sketch, "E118", {"start": v(13.89, -9.2) * mm, "end": v(15.02, -9.2) * mm});
            skLineSegment(sketch, "E119", {"start": v(15.02, -9.2) * mm, "end": v(15.02, -8.55) * mm});
            skLineSegment(sketch, "E120", {"start": v(15.02, -8.55) * mm, "end": v(14.33, -8.55) * mm});
            skLineSegment(sketch, "E121", {"start": v(14.33, -8.55) * mm, "end": v(12.3, -6.45) * mm});
            skLineSegment(sketch, "E122", {"start": v(12.3, -6.45) * mm, "end": v(12.3, -5.74) * mm});
            skLineSegment(sketch, "E123", {"start": v(12.3, -5.74) * mm, "end": v(11.48, -5.74) * mm});
            skLineSegment(sketch, "E124", {"start": v(16.56, -8.59) * mm, "end": v(17.66, -8.59) * mm});
            skLineSegment(sketch, "E125", {"start": v(17.66, -8.59) * mm, "end": v(18.38, -7.87) * mm});
            skLineSegment(sketch, "E126", {"start": v(18.38, -7.87) * mm, "end": v(18.38, -4.67) * mm});
            skLineSegment(sketch, "E127", {"start": v(19.13, -3.95) * mm, "end": v(19.96, -3.95) * mm});
            skLineSegment(sketch, "E128", {"start": v(19.96, -3.95) * mm, "end": v(19.96, -4.58) * mm});
            skLineSegment(sketch, "E129", {"start": v(19.96, -4.58) * mm, "end": v(19.38, -4.58) * mm});
            skLineSegment(sketch, "E130", {"start": v(19.38, -4.58) * mm, "end": v(19.1, -4.86) * mm});
            skLineSegment(sketch, "E131", {"start": v(19.1, -8.15) * mm, "end": v(17.99, -9.3) * mm});
            skLineSegment(sketch, "E132", {"start": v(17.99, -9.3) * mm, "end": v(16.56, -9.3) * mm});
            skLineSegment(sketch, "E133", {"start": v(16.56, -9.3) * mm, "end": v(16.56, -8.59) * mm});
            skLineSegment(sketch, "E134", {"start": v(16.56, -3.02) * mm, "end": v(19.98, -3.02) * mm});
            skLineSegment(sketch, "E135", {"start": v(19.98, -3.02) * mm, "end": v(19.98, -2.34) * mm});
            skLineSegment(sketch, "E136", {"start": v(19.98, -2.34) * mm, "end": v(16.56, -2.34) * mm});
            skLineSegment(sketch, "E137", {"start": v(16.56, -2.34) * mm, "end": v(16.56, -3.02) * mm});
            skLineSegment(sketch, "E138", {"start": v(8.31, -1.98) * mm, "end": v(8.31, -0.7) * mm});
            skLineSegment(sketch, "E139", {"start": v(8.31, -0.7) * mm, "end": v(7.82, -0.27) * mm});
            skLineSegment(sketch, "E140", {"start": v(7.82, -0.27) * mm, "end": v(4.2, -0.27) * mm});
            skLineSegment(sketch, "E141", {"start": v(4.2, -0.27) * mm, "end": v(3.69, 0.15) * mm});
            skLineSegment(sketch, "E142", {"start": v(3.69, 0.15) * mm, "end": v(3.69, 0.47) * mm});
            skLineSegment(sketch, "E143", {"start": v(3.69, 0.47) * mm, "end": v(3.2, 0.47) * mm});
            skLineSegment(sketch, "E144", {"start": v(3.2, 0.47) * mm, "end": v(3.2, 0) * mm});
            skLineSegment(sketch, "E145", {"start": v(3.2, 0) * mm, "end": v(4.12, -0.73) * mm});
            skLineSegment(sketch, "E146", {"start": v(4.12, -0.73) * mm, "end": v(7.69, -0.73) * mm});
            skLineSegment(sketch, "E147", {"start": v(7.69, -0.73) * mm, "end": v(7.92, -1) * mm});
            skLineSegment(sketch, "E148", {"start": v(7.92, -1) * mm, "end": v(7.92, -1.98) * mm});
            skLineSegment(sketch, "E149", {"start": v(7.92, -1.98) * mm, "end": v(8.31, -1.98) * mm});
            skLineSegment(sketch, "E150", {"start": v(2.78, -2.39) * mm, "end": v(2.24, -1.98) * mm});
            skLineSegment(sketch, "E151", {"start": v(2.24, -1.98) * mm, "end": v(2.24, -0.5) * mm});
            skLineSegment(sketch, "E152", {"start": v(2.24, -0.5) * mm, "end": v(1, 0.74) * mm});
            skLineSegment(sketch, "E153", {"start": v(1, 0.74) * mm, "end": v(0.2, 0.74) * mm});
            skLineSegment(sketch, "E154", {"start": v(0.2, 0.4) * mm, "end": v(0.85, 0.4) * mm});
            skLineSegment(sketch, "E155", {"start": v(2.69, 0.95) * mm, "end": v(2.24, 0.95) * mm});
            skLineSegment(sketch, "E156", {"start": v(2.24, 0.95) * mm, "end": v(1.03, 2.15) * mm});
            skLineSegment(sketch, "E157", {"start": v(1.03, 2.15) * mm, "end": v(0.22, 2.15) * mm});
            skLineSegment(sketch, "E158", {"start": v(0.22, 2.15) * mm, "end": v(0.22, 2.52) * mm});
            skLineSegment(sketch, "E159", {"start": v(0.22, 2.52) * mm, "end": v(1.1, 2.52) * mm});
            skLineSegment(sketch, "E160", {"start": v(1.1, 2.52) * mm, "end": v(2.3, 1.32) * mm});
            skLineSegment(sketch, "E161", {"start": v(2.3, 1.32) * mm, "end": v(2.69, 1.32) * mm});
            skLineSegment(sketch, "E162", {"start": v(2.69, 1.32) * mm, "end": v(2.69, 0.95) * mm});
            skLineSegment(sketch, "E163", {"start": v(8.8, 5.7) * mm, "end": v(10.04, 5.7) * mm});
            skLineSegment(sketch, "E164", {"start": v(10.04, 5.7) * mm, "end": v(10.76, 5.13) * mm});
            skLineSegment(sketch, "E165", {"start": v(10.76, 5.13) * mm, "end": v(10.76, 3.78) * mm});
            skLineSegment(sketch, "E166", {"start": v(10.76, 3.78) * mm, "end": v(11.2, 3.78) * mm});
            skLineSegment(sketch, "E167", {"start": v(11.2, 3.78) * mm, "end": v(11.2, 5.2) * mm});
            skLineSegment(sketch, "E168", {"start": v(11.2, 5.2) * mm, "end": v(10.13, 6.04) * mm});
            skLineSegment(sketch, "E169", {"start": v(10.13, 6.04) * mm, "end": v(8.8, 6.04) * mm});
            skLineSegment(sketch, "E170", {"start": v(8.8, 6.04) * mm, "end": v(8.8, 5.7) * mm});
            skLineSegment(sketch, "E171", {"start": v(11.38, 1.19) * mm, "end": v(15.05, 1.19) * mm});
            skLineSegment(sketch, "E172", {"start": v(15.05, 1.19) * mm, "end": v(15.05, 1.63) * mm});
            skLineSegment(sketch, "E173", {"start": v(15.05, 1.63) * mm, "end": v(11.38, 1.63) * mm});
            skLineSegment(sketch, "E174", {"start": v(11.38, 1.63) * mm, "end": v(11.38, 1.19) * mm});
            skLineSegment(sketch, "E175", {"start": v(16.57, 1.19) * mm, "end": v(18.08, 1.19) * mm});
            skLineSegment(sketch, "E176", {"start": v(18.76, 2.28) * mm, "end": v(19.98, 2.3) * mm});
            skLineSegment(sketch, "E177", {"start": v(19.98, 2.3) * mm, "end": v(19.98, 2.88) * mm});
            skLineSegment(sketch, "E178", {"start": v(16.57, 1.8) * mm, "end": v(16.57, 1.19) * mm});
            skLineSegment(sketch, "E179", {"start": v(19.98, 2.88) * mm, "end": v(18.5, 2.88) * mm});
            skLineSegment(sketch, "E180", {"start": v(17.82, 1.8) * mm, "end": v(16.57, 1.8) * mm});
            skLineSegment(sketch, "E181", {"start": v(-22.8, -18.45) * mm, "end": v(-22.8, -19.74) * mm});
            skLineSegment(sketch, "E182", {"start": v(-26.53, -18.45) * mm, "end": v(-26.53, -19.74) * mm});
            skLineSegment(sketch, "E183", {"start": v(-20.57, -6.96) * mm, "end": v(-22.04, -6.96) * mm});
            skLineSegment(sketch, "E184", {"start": v(-22.04, -6.96) * mm, "end": v(-22.04, -5.7) * mm});
            skLineSegment(sketch, "E185", {"start": v(-22.04, -5.7) * mm, "end": v(-20.57, -5.7) * mm});
            skLineSegment(sketch, "E186", {"start": v(-20.57, -5.7) * mm, "end": v(-20.57, -6.96) * mm});
            skLineSegment(sketch, "E187", {"start": v(-26.63, -6.96) * mm, "end": v(-28.36, -6.96) * mm});
            skLineSegment(sketch, "E188", {"start": v(-28.36, -6.96) * mm, "end": v(-28.36, -5.69) * mm});
            skLineSegment(sketch, "E189", {"start": v(-28.36, -5.69) * mm, "end": v(-26.63, -5.69) * mm});
            skLineSegment(sketch, "E190", {"start": v(-26.63, -5.69) * mm, "end": v(-26.63, -6.96) * mm});
            skLineSegment(sketch, "E191", {"start": v(-18.92, -10.81) * mm, "end": v(-20.1, -10.81) * mm});
            skLineSegment(sketch, "E192", {"start": v(-20.1, -10.81) * mm, "end": v(-20.1, -12.1) * mm});
            skLineSegment(sketch, "E193", {"start": v(-20.1, -12.1) * mm, "end": v(-18.92, -12.1) * mm});
            skLineSegment(sketch, "E194", {"start": v(-18.92, -12.1) * mm, "end": v(-18.92, -10.81) * mm});
            skLineSegment(sketch, "E195", {"start": v(-18.95, -15.93) * mm, "end": v(-20.03, -15.93) * mm});
            skLineSegment(sketch, "E196", {"start": v(-20.03, -15.93) * mm, "end": v(-20.03, -14.62) * mm});
            skLineSegment(sketch, "E197", {"start": v(-20.03, -14.62) * mm, "end": v(-18.95, -14.62) * mm});
            skLineSegment(sketch, "E198", {"start": v(-18.95, -14.62) * mm, "end": v(-18.95, -15.93) * mm});
            skLineSegment(sketch, "E199", {"start": v(-18.94, -15.87) * mm, "end": v(-18.95, -15.93) * mm});
            skLineSegment(sketch, "E200", {"start": v(-22.8, -18.45) * mm, "end": v(-21.57, -18.45) * mm});
            skLineSegment(sketch, "E201", {"start": v(-21.57, -18.45) * mm, "end": v(-21.57, -19.75) * mm});
            skLineSegment(sketch, "E202", {"start": v(-21.57, -19.75) * mm, "end": v(-22.8, -19.74) * mm});
            skLineSegment(sketch, "E203", {"start": v(-26.53, -18.45) * mm, "end": v(-27.96, -18.45) * mm});
            skLineSegment(sketch, "E204", {"start": v(-27.96, -18.45) * mm, "end": v(-27.96, -19.73) * mm});
            skLineSegment(sketch, "E205", {"start": v(-27.96, -19.73) * mm, "end": v(-26.53, -19.74) * mm});
            skLineSegment(sketch, "E206", {"start": v(-18.92, -18.38) * mm, "end": v(-20.05, -18.38) * mm});
            skLineSegment(sketch, "E207", {"start": v(-20.05, -18.38) * mm, "end": v(-20.05, -19.64) * mm});
            skLineSegment(sketch, "E208", {"start": v(-20.05, -19.64) * mm, "end": v(-18.92, -19.64) * mm});
            skLineSegment(sketch, "E209", {"start": v(-15.23, -18.41) * mm, "end": v(-13.96, -18.41) * mm});
            skLineSegment(sketch, "E210", {"start": v(-13.96, -18.41) * mm, "end": v(-13.96, -19.75) * mm});
            skLineSegment(sketch, "E211", {"start": v(-13.96, -19.75) * mm, "end": v(-15.23, -19.75) * mm});
            skLineSegment(sketch, "E212", {"start": v(-15.23, -19.75) * mm, "end": v(-15.23, -18.41) * mm});
            skLineSegment(sketch, "E213", {"start": v(-6.12, -15.36) * mm, "end": v(-6.12, -14.42) * mm});
            skLineSegment(sketch, "E214", {"start": v(-6.12, -14.42) * mm, "end": v(-6.7, -14.42) * mm});
            skLineSegment(sketch, "E215", {"start": v(-6.7, -14.42) * mm, "end": v(-6.73, -15.36) * mm});
            skLineSegment(sketch, "E216", {"start": v(-8.06, -15.07) * mm, "end": v(-8.06, -13.64) * mm});
            skLineSegment(sketch, "E217", {"start": v(-8.06, -13.64) * mm, "end": v(-8.87, -13.64) * mm});
            skLineSegment(sketch, "E218", {"start": v(-8.87, -13.64) * mm, "end": v(-8.87, -14.57) * mm});
            skLineSegment(sketch, "E219", {"start": v(-8.87, -14.57) * mm, "end": v(-8.86, -14.57) * mm});
            skLineSegment(sketch, "E220", {"start": v(-8.86, -14.57) * mm, "end": v(-8.85, -15.07) * mm});
            skLineSegment(sketch, "E221", {"start": v(-15.35, -10.66) * mm, "end": v(-15.35, -9.4) * mm});
            skLineSegment(sketch, "E222", {"start": v(-15.35, -9.4) * mm, "end": v(-16.55, -9.4) * mm});
            skLineSegment(sketch, "E223", {"start": v(-16.55, -9.4) * mm, "end": v(-16.55, -10.66) * mm});
            skLineSegment(sketch, "E224", {"start": v(-16.55, -10.66) * mm, "end": v(-15.32, -10.66) * mm});
            skLineSegment(sketch, "E225", {"start": v(-13.14, -10.91) * mm, "end": v(-14.25, -10.91) * mm});
            skLineSegment(sketch, "E226", {"start": v(-14.25, -10.91) * mm, "end": v(-14.25, -9.6) * mm});
            skLineSegment(sketch, "E227", {"start": v(-14.25, -9.6) * mm, "end": v(-13.14, -9.6) * mm});
            skLineSegment(sketch, "E228", {"start": v(-13.14, -9.6) * mm, "end": v(-13.14, -10.91) * mm});
            skLineSegment(sketch, "E229", {"start": v(-8.43, -21.78) * mm, "end": v(-6.86, -21.78) * mm});
            skLineSegment(sketch, "E230", {"start": v(-6.86, -21.78) * mm, "end": v(-6.86, -23) * mm});
            skLineSegment(sketch, "E231", {"start": v(-6.86, -23) * mm, "end": v(-8.43, -23) * mm});
            skLineSegment(sketch, "E232", {"start": v(-8.43, -23) * mm, "end": v(-8.43, -21.78) * mm});
            skLineSegment(sketch, "E233", {"start": v(-3.03, -11.85) * mm, "end": v(-4.52, -11.85) * mm});
            skLineSegment(sketch, "E234", {"start": v(-4.52, -11.85) * mm, "end": v(-4.52, -10.69) * mm});
            skLineSegment(sketch, "E235", {"start": v(-4.52, -10.69) * mm, "end": v(-3.03, -10.69) * mm});
            skLineSegment(sketch, "E236", {"start": v(-3.03, -10.69) * mm, "end": v(-3.03, -11.85) * mm});
            skLineSegment(sketch, "E237", {"start": v(0.78, -20.36) * mm, "end": v(0.78, -21.88) * mm});
            skLineSegment(sketch, "E238", {"start": v(0.78, -21.88) * mm, "end": v(-0.53, -21.88) * mm});
            skLineSegment(sketch, "E239", {"start": v(-0.53, -21.88) * mm, "end": v(-0.53, -20.36) * mm});
            skLineSegment(sketch, "E240", {"start": v(-0.53, -20.36) * mm, "end": v(0.78, -20.36) * mm});
            skLineSegment(sketch, "E241", {"start": v(6.3, -22.2) * mm, "end": v(4.74, -22.2) * mm});
            skLineSegment(sketch, "E242", {"start": v(4.74, -22.2) * mm, "end": v(4.74, -20.9) * mm});
            skLineSegment(sketch, "E243", {"start": v(4.74, -20.9) * mm, "end": v(6.3, -20.9) * mm});
            skLineSegment(sketch, "E244", {"start": v(6.3, -20.9) * mm, "end": v(6.3, -22.2) * mm});
            skLineSegment(sketch, "E245", {"start": v(25.2, -22.2) * mm, "end": v(26.46, -22.2) * mm});
            skLineSegment(sketch, "E246", {"start": v(26.46, -22.2) * mm, "end": v(26.46, -21) * mm});
            skLineSegment(sketch, "E247", {"start": v(26.46, -21) * mm, "end": v(25.2, -21) * mm});
            skLineSegment(sketch, "E248", {"start": v(25.2, -21) * mm, "end": v(25.2, -22.2) * mm});
            skLineSegment(sketch, "E249", {"start": v(25.2, -15.88) * mm, "end": v(26.58, -15.88) * mm});
            skLineSegment(sketch, "E250", {"start": v(26.58, -15.88) * mm, "end": v(26.58, -14.63) * mm});
            skLineSegment(sketch, "E251", {"start": v(26.58, -14.63) * mm, "end": v(25.2, -14.63) * mm});
            skLineSegment(sketch, "E252", {"start": v(25.2, -14.63) * mm, "end": v(25.2, -15.88) * mm});
            skLineSegment(sketch, "E253", {"start": v(16.47, -12.1) * mm, "end": v(16.47, -13.34) * mm});
            skLineSegment(sketch, "E254", {"start": v(16.47, -13.34) * mm, "end": v(15.2, -13.34) * mm});
            skLineSegment(sketch, "E255", {"start": v(15.2, -13.34) * mm, "end": v(15.2, -12.1) * mm});
            skLineSegment(sketch, "E256", {"start": v(15.2, -12.1) * mm, "end": v(16.47, -12.1) * mm});
            skLineSegment(sketch, "E257", {"start": v(8.66, -5.56) * mm, "end": v(8.66, -6.96) * mm});
            skLineSegment(sketch, "E258", {"start": v(8.66, -6.96) * mm, "end": v(7.5, -6.96) * mm});
            skLineSegment(sketch, "E259", {"start": v(7.5, -6.96) * mm, "end": v(7.5, -5.56) * mm});
            skLineSegment(sketch, "E260", {"start": v(7.5, -5.56) * mm, "end": v(8.66, -5.56) * mm});
            skLineSegment(sketch, "E261", {"start": v(4.07, -5.72) * mm, "end": v(4.07, -6.92) * mm});
            skLineSegment(sketch, "E262", {"start": v(4.07, -6.92) * mm, "end": v(2.94, -6.92) * mm});
            skLineSegment(sketch, "E263", {"start": v(2.94, -6.92) * mm, "end": v(2.94, -5.72) * mm});
            skLineSegment(sketch, "E264", {"start": v(2.94, -5.72) * mm, "end": v(4.07, -5.72) * mm});
            skLineSegment(sketch, "E265", {"start": v(4.26, -3.38) * mm, "end": v(5.92, -3.38) * mm});
            skLineSegment(sketch, "E266", {"start": v(5.92, -3.38) * mm, "end": v(5.92, -2.21) * mm});
            skLineSegment(sketch, "E267", {"start": v(5.92, -2.21) * mm, "end": v(4.26, -2.21) * mm});
            skLineSegment(sketch, "E268", {"start": v(7.56, 1.64) * mm, "end": v(6.32, 1.64) * mm});
            skLineSegment(sketch, "E269", {"start": v(6.32, 1.64) * mm, "end": v(6.3, 1.63) * mm});
            skLineSegment(sketch, "E270", {"start": v(6.3, 1.63) * mm, "end": v(6.3, 0.49) * mm});
            skLineSegment(sketch, "E271", {"start": v(6.3, 0.49) * mm, "end": v(6.98, 0.49) * mm});
            skLineSegment(sketch, "E272", {"start": v(6.98, 0.49) * mm, "end": v(6.98, 1.21) * mm});
            skLineSegment(sketch, "E273", {"start": v(6.98, 1.21) * mm, "end": v(7.56, 1.2) * mm});
            skLineSegment(sketch, "E274", {"start": v(7.65, 2.18) * mm, "end": v(5.32, 2.18) * mm});
            skLineSegment(sketch, "E275", {"start": v(5.32, 2.18) * mm, "end": v(5.32, 2.77) * mm});
            skLineSegment(sketch, "E276", {"start": v(5.32, 2.77) * mm, "end": v(7.65, 2.78) * mm});
            skLineSegment(sketch, "E277", {"start": v(11.41, 2.76) * mm, "end": v(12.93, 2.76) * mm});
            skLineSegment(sketch, "E278", {"start": v(12.93, 2.76) * mm, "end": v(12.93, 2.18) * mm});
            skLineSegment(sketch, "E279", {"start": v(12.93, 2.18) * mm, "end": v(11.41, 2.2) * mm});
            skLineSegment(sketch, "E280", {"start": v(7.57, 3.34) * mm, "end": v(6.32, 3.34) * mm});
            skLineSegment(sketch, "E281", {"start": v(6.32, 3.34) * mm, "end": v(6.3, 3.36) * mm});
            skLineSegment(sketch, "E282", {"start": v(6.3, 3.36) * mm, "end": v(6.29, 4.55) * mm});
            skLineSegment(sketch, "E283", {"start": v(6.29, 4.55) * mm, "end": v(7.02, 4.55) * mm});
            skLineSegment(sketch, "E284", {"start": v(7.02, 4.55) * mm, "end": v(7.02, 3.73) * mm});
            skLineSegment(sketch, "E285", {"start": v(7.02, 3.73) * mm, "end": v(7.57, 3.73) * mm});
            skLineSegment(sketch, "E286", {"start": v(7.57, 3.73) * mm, "end": v(7.57, 3.34) * mm});
            skLineSegment(sketch, "E287", {"start": v(4.06, 4.23) * mm, "end": v(4.06, 5.99) * mm});
            skLineSegment(sketch, "E288", {"start": v(4.06, 5.99) * mm, "end": v(2.84, 5.98) * mm});
            skLineSegment(sketch, "E289", {"start": v(2.84, 5.98) * mm, "end": v(2.85, 4.23) * mm});
            skLineSegment(sketch, "E290", {"start": v(2.85, 4.23) * mm, "end": v(4.06, 4.23) * mm});
            skLineSegment(sketch, "E291", {"start": v(16.48, 4.36) * mm, "end": v(16.47, 5.95) * mm});
            skLineSegment(sketch, "E292", {"start": v(16.47, 5.95) * mm, "end": v(15.04, 5.95) * mm});
            skLineSegment(sketch, "E293", {"start": v(15.04, 5.95) * mm, "end": v(15.05, 4.36) * mm});
            skLineSegment(sketch, "E294", {"start": v(11.35, -1.98) * mm, "end": v(11.35, -0.17) * mm});
            skLineSegment(sketch, "E295", {"start": v(11.35, -0.17) * mm, "end": v(12.6, -0.17) * mm});
            skLineSegment(sketch, "E296", {"start": v(12.6, -0.17) * mm, "end": v(12.6, -1.98) * mm});
            skLineSegment(sketch, "E297", {"start": v(12.6, -1.98) * mm, "end": v(11.35, -1.98) * mm});
            skLineSegment(sketch, "E298", {"start": v(15.14, -1.98) * mm, "end": v(15.13, -0.33) * mm});
            skLineSegment(sketch, "E299", {"start": v(15.13, -0.33) * mm, "end": v(16.44, -0.33) * mm});
            skLineSegment(sketch, "E300", {"start": v(16.44, -0.33) * mm, "end": v(16.44, -1.98) * mm});
            skLineSegment(sketch, "E301", {"start": v(16.44, -1.98) * mm, "end": v(15.14, -1.98) * mm});
            skLineSegment(sketch, "E302", {"start": v(22.23, 0.32) * mm, "end": v(24.09, 0.32) * mm});
            skLineSegment(sketch, "E303", {"start": v(24.09, 0.32) * mm, "end": v(24.09, 1.22) * mm});
            skLineSegment(sketch, "E304", {"start": v(24.09, 1.22) * mm, "end": v(22.23, 1.22) * mm});
            skLineSegment(sketch, "E305", {"start": v(22.23, 1.22) * mm, "end": v(22.23, 0.32) * mm});
            skLineSegment(sketch, "E306", {"start": v(22.27, -0.54) * mm, "end": v(23.82, -0.54) * mm});
            skLineSegment(sketch, "E307", {"start": v(23.82, -0.54) * mm, "end": v(23.82, -1.47) * mm});
            skLineSegment(sketch, "E308", {"start": v(23.82, -1.47) * mm, "end": v(22.27, -1.47) * mm});
            skLineSegment(sketch, "E309", {"start": v(22.27, -1.47) * mm, "end": v(22.27, -0.54) * mm});
            skLineSegment(sketch, "E310", {"start": v(16.47, -5.7) * mm, "end": v(16.47, -6.93) * mm});
            skLineSegment(sketch, "E311", {"start": v(16.47, -6.93) * mm, "end": v(15.1, -6.93) * mm});
            skLineSegment(sketch, "E312", {"start": v(15.1, -6.93) * mm, "end": v(15.1, -5.7) * mm});
            skLineSegment(sketch, "E313", {"start": v(15.1, -5.7) * mm, "end": v(16.47, -5.7) * mm});
            skLineSegment(sketch, "E314", {"start": v(-20.57, 4.63) * mm, "end": v(-22.28, 4.63) * mm});
            skLineSegment(sketch, "E315", {"start": v(-22.28, 4.63) * mm, "end": v(-22.28, 5.87) * mm});
            skLineSegment(sketch, "E316", {"start": v(-22.28, 5.87) * mm, "end": v(-20.57, 5.87) * mm});
            skLineSegment(sketch, "E317", {"start": v(-20.57, 5.87) * mm, "end": v(-20.57, 4.63) * mm});
            skLineSegment(sketch, "E318", {"start": v(-26.63, 4.63) * mm, "end": v(-28.2, 4.63) * mm});
            skLineSegment(sketch, "E319", {"start": v(-28.2, 4.63) * mm, "end": v(-28.2, 6.01) * mm});
            skLineSegment(sketch, "E320", {"start": v(-28.2, 6.01) * mm, "end": v(-26.63, 6.01) * mm});
            skLineSegment(sketch, "E321", {"start": v(-26.63, 6.01) * mm, "end": v(-26.63, 4.63) * mm});
            skLineSegment(sketch, "E322", {"start": v(6.45, 6.7) * mm, "end": v(6.45, 8.2) * mm});
            skLineSegment(sketch, "E323", {"start": v(6.45, 8.2) * mm, "end": v(5.15, 8.19) * mm});
            skLineSegment(sketch, "E324", {"start": v(5.15, 8.19) * mm, "end": v(5.16, 6.7) * mm});
            skLineSegment(sketch, "E325", {"start": v(5.16, 6.7) * mm, "end": v(6.45, 6.7) * mm});
            skLineSegment(sketch, "E326", {"start": v(6.35, -15.9) * mm, "end": v(4.87, -15.9) * mm});
            skLineSegment(sketch, "E327", {"start": v(4.87, -15.9) * mm, "end": v(4.87, -14.62) * mm});
            skLineSegment(sketch, "E328", {"start": v(4.87, -14.62) * mm, "end": v(6.35, -14.61) * mm});
            skLineSegment(sketch, "E329", {"start": v(6.35, -14.61) * mm, "end": v(6.35, -15.9) * mm});
            skLineSegment(sketch, "E330", {"start": v(-1.94, -4.87) * mm, "end": v(-3.77, -4.88) * mm});
            skLineSegment(sketch, "E331", {"start": v(-3.77, -4.88) * mm, "end": v(-3.77, -3.97) * mm});
            skLineSegment(sketch, "E332", {"start": v(-3.77, -3.97) * mm, "end": v(-1.94, -3.96) * mm});
            skLineSegment(sketch, "E333", {"start": v(-1.94, -3.96) * mm, "end": v(-1.94, -4.87) * mm});
            skLineSegment(sketch, "E334", {"start": v(-1.96, -3.2) * mm, "end": v(-3.73, -3.2) * mm});
            skLineSegment(sketch, "E335", {"start": v(-3.73, -3.2) * mm, "end": v(-3.73, -2.27) * mm});
            skLineSegment(sketch, "E336", {"start": v(-3.73, -2.27) * mm, "end": v(-1.96, -2.27) * mm});
            skLineSegment(sketch, "E337", {"start": v(-1.96, -2.27) * mm, "end": v(-1.96, -3.2) * mm});
            skLineSegment(sketch, "E338", {"start": v(-1.96, -1.5) * mm, "end": v(-3.7, -1.51) * mm});
            skLineSegment(sketch, "E339", {"start": v(-3.7, -1.51) * mm, "end": v(-3.7, -0.65) * mm});
            skLineSegment(sketch, "E340", {"start": v(-3.7, -0.65) * mm, "end": v(-1.96, -0.64) * mm});
            skLineSegment(sketch, "E341", {"start": v(-1.96, -0.64) * mm, "end": v(-1.96, -1.5) * mm});
            skLineSegment(sketch, "E342", {"start": v(4.26, -3.48) * mm, "end": v(4.26, -3.38) * mm});
            skLineSegment(sketch, "E343", {"start": v(4.26, -2.21) * mm, "end": v(4.26, -1.98) * mm});
            skLineSegment(sketch, "E344", {"start": v(0.2, 0.15) * mm, "end": v(0.2, 0.4) * mm});
            skLineSegment(sketch, "E345", {"start": v(2.78, -2.39) * mm, "end": v(2.78, -1.98) * mm});
            skLineSegment(sketch, "E346", {"start": v(0.2, 0.74) * mm, "end": v(0.2, 1.18) * mm});
            skLineSegment(sketch, "E347", {"start": v(2.78, -2.9) * mm, "end": v(1.85, -2.2) * mm});
            skLineSegment(sketch, "E348", {"start": v(1.85, -2.2) * mm, "end": v(1.85, -0.54) * mm});
            skLineSegment(sketch, "E349", {"start": v(1.85, -0.54) * mm, "end": v(0.85, 0.4) * mm});
            skLineSegment(sketch, "E350", {"start": v(2.78, -3.48) * mm, "end": v(2.78, -2.9) * mm});
            skCircle(sketch, "E351", {"center": v(-21.56, -6.4) * mm, "radius": 0.3 * mm});
            skCircle(sketch, "E352", {"center": v(-27.9, -6.4) * mm, "radius": 0.3 * mm});
            skLineSegment(sketch, "E353", {"start": v(-6.5, -16.57) * mm, "end": v(-7.94, -16.57) * mm});
            skLineSegment(sketch, "E354", {"start": v(-7.94, -16.57) * mm, "end": v(-7.94, -16.11) * mm});
            skLineSegment(sketch, "E355", {"start": v(21.5, -14.65) * mm, "end": v(10.04, -14.65) * mm});
            skLineSegment(sketch, "E356", {"start": v(21.5, -15.22) * mm, "end": v(21.5, -14.65) * mm});
            skLineSegment(sketch, "E357", {"start": v(10.09, -21.02) * mm, "end": v(21.47, -21.02) * mm});
            skLineSegment(sketch, "E358", {"start": v(21.47, -21.02) * mm, "end": v(21.47, -21.54) * mm});
            skLineSegment(sketch, "E359", {"start": v(10.09, -21.02) * mm, "end": v(10.09, -21.54) * mm});
            skLineSegment(sketch, "E360", {"start": v(-11.67, -17.55) * mm, "end": v(-11.67, -21.7) * mm});
            skLineSegment(sketch, "E361", {"start": v(-11.67, -21.7) * mm, "end": v(-11.33, -21.7) * mm});
            skLineSegment(sketch, "E362", {"start": v(-11.33, -17.55) * mm, "end": v(-11.67, -17.55) * mm});
            skLineSegment(sketch, "E363", {"start": v(19.1, -8.15) * mm, "end": v(19.1, -4.86) * mm});
            skLineSegment(sketch, "E364", {"start": v(19.13, -3.95) * mm, "end": v(18.38, -4.67) * mm});
            skLineSegment(sketch, "E365", {"start": v(17.82, 1.8) * mm, "end": v(18.5, 2.88) * mm});
            skLineSegment(sketch, "E366", {"start": v(18.08, 1.19) * mm, "end": v(18.76, 2.28) * mm});
            skLineSegment(sketch, "E367", {"start": v(-11.57, -13.42) * mm, "end": v(-11.57, -15.04) * mm});
            skLineSegment(sketch, "E368", {"start": v(1.74, -14.64) * mm, "end": v(1.74, -12.03) * mm});
            skLineSegment(sketch, "E369", {"start": v(1.74, -12.03) * mm, "end": v(0.7, -12.03) * mm});
            skLineSegment(sketch, "E370", {"start": v(0.7, -11.17) * mm, "end": v(0.7, -12.03) * mm});
            skLineSegment(sketch, "E371", {"start": v(-16.56, -12.26) * mm, "end": v(-16.56, -14.4) * mm});
            skLineSegment(sketch, "E372", {"start": v(-16.56, -14.4) * mm, "end": v(-15.3, -14.4) * mm});
            skSolve(sketch);
        }
        {
            var Q0;
            Q0=qCreatedBy(makeId("Top.planeOp"),FACE);
            var sketch = newSketch(context, id + "F1", { "sketchPlane" : qUnion([Q0])});
            skLineSegment(sketch, "E373.bottom", {"start": v(-31.07, 17.75) * mm, "end": v(37.5, 17.75) * mm});
            skLineSegment(sketch, "E373.top", {"start": v(-31.07, -35.6) * mm, "end": v(37.5, -35.6) * mm});
            skLineSegment(sketch, "E373.left", {"start": v(-31.07, 17.75) * mm, "end": v(-31.07, -35.6) * mm});
            skLineSegment(sketch, "E373.right", {"start": v(37.5, 17.75) * mm, "end": v(37.5, -35.6) * mm});
            skCircle(sketch, "E374", {"center": v(-25.13, -29.5) * mm, "radius": 1.71 * mm});
            skCircle(sketch, "E375", {"center": v(-25.13, -29.5) * mm, "radius": 3.05 * mm});
            skCircle(sketch, "E376", {"center": v(31.46, -29.5) * mm, "radius": 1.71 * mm});
            skCircle(sketch, "E377", {"center": v(31.46, -29.5) * mm, "radius": 3.05 * mm});
            skCircle(sketch, "E378", {"center": v(31.46, 11.86) * mm, "radius": 1.71 * mm});
            skCircle(sketch, "E379", {"center": v(31.46, 11.86) * mm, "radius": 3.05 * mm});
            skCircle(sketch, "E380", {"center": v(-25.13, 11.86) * mm, "radius": 1.71 * mm});
            skCircle(sketch, "E381", {"center": v(-25.13, 11.86) * mm, "radius": 3.05 * mm});
            skCircle(sketch, "E382", {"center": v(-25.32, -0.53) * mm, "radius": 0.82 * mm});
            skCircle(sketch, "E383", {"center": v(-25.32, -0.53) * mm, "radius": 1.33 * mm});
            skCircle(sketch, "E384", {"center": v(-20.86, -0.53) * mm, "radius": 0.83 * mm});
            skCircle(sketch, "E385", {"center": v(-20.86, -0.53) * mm, "radius": 1.33 * mm});
            skLineSegment(sketch, "E386.top", {"start": v(-27.3, -14.78) * mm, "end": v(-24.56, -14.78) * mm});
            skLineSegment(sketch, "E386.left", {"start": v(-27.3, -13.18) * mm, "end": v(-27.3, -14.78) * mm});
            skLineSegment(sketch, "E386.right", {"start": v(-24.56, -13.17) * mm, "end": v(-24.56, -14.78) * mm});
            skLineSegment(sketch, "E387.bottom", {"start": v(-26.46, -13.18) * mm, "end": v(-25.4, -13.18) * mm});
            skLineSegment(sketch, "E387.top", {"start": v(-26.46, -14.16) * mm, "end": v(-25.4, -14.16) * mm});
            skLineSegment(sketch, "E387.left", {"start": v(-26.46, -13.18) * mm, "end": v(-26.46, -14.16) * mm});
            skLineSegment(sketch, "E387.right", {"start": v(-25.4, -13.18) * mm, "end": v(-25.4, -14.16) * mm});
            skLineSegment(sketch, "E388", {"start": v(-27.3, -13.18) * mm, "end": v(-26.46, -13.18) * mm});
            skLineSegment(sketch, "E389", {"start": v(-24.56, -13.17) * mm, "end": v(-25.4, -13.18) * mm});
            skLineSegment(sketch, "E390.bottom", {"start": v(-17.98, -29.84) * mm, "end": v(-19.13, -29.84) * mm});
            skLineSegment(sketch, "E390.top", {"start": v(-17.98, -28.67) * mm, "end": v(-19.13, -28.67) * mm});
            skLineSegment(sketch, "E390.left", {"start": v(-17.98, -29.84) * mm, "end": v(-17.98, -28.67) * mm});
            skLineSegment(sketch, "E390.right", {"start": v(-19.13, -29.84) * mm, "end": v(-19.13, -28.67) * mm});
            skPoint(sketch, "E390.middle", {"position": v(-18.56, -29.25) * mm});
            skLineSegment(sketch, "E391.bottom", {"start": v(-15.38, -29.83) * mm, "end": v(-16.54, -29.83) * mm});
            skLineSegment(sketch, "E391.top", {"start": v(-15.38, -28.68) * mm, "end": v(-16.54, -28.68) * mm});
            skLineSegment(sketch, "E391.left", {"start": v(-15.38, -29.83) * mm, "end": v(-15.38, -28.68) * mm});
            skLineSegment(sketch, "E391.right", {"start": v(-16.54, -29.83) * mm, "end": v(-16.54, -28.68) * mm});
            skPoint(sketch, "E391.middle", {"position": v(-15.96, -29.25) * mm});
            skLineSegment(sketch, "E392.right", {"start": v(-17.04, -30.34) * mm, "end": v(-17.04, -28.16) * mm});
            skLineSegment(sketch, "E393.bottom", {"start": v(-12.7, -29.82) * mm, "end": v(-13.85, -29.82) * mm});
            skLineSegment(sketch, "E393.top", {"start": v(-12.7, -28.69) * mm, "end": v(-13.85, -28.69) * mm});
            skLineSegment(sketch, "E393.left", {"start": v(-12.7, -29.82) * mm, "end": v(-12.7, -28.69) * mm});
            skLineSegment(sketch, "E393.right", {"start": v(-13.85, -29.82) * mm, "end": v(-13.85, -28.69) * mm});
            skPoint(sketch, "E393.middle", {"position": v(-13.28, -29.25) * mm});
            skLineSegment(sketch, "E394.bottom", {"start": v(-10.1, -29.82) * mm, "end": v(-11.22, -29.82) * mm});
            skLineSegment(sketch, "E394.top", {"start": v(-10.1, -28.69) * mm, "end": v(-11.22, -28.69) * mm});
            skLineSegment(sketch, "E394.left", {"start": v(-10.1, -29.82) * mm, "end": v(-10.1, -28.69) * mm});
            skLineSegment(sketch, "E394.right", {"start": v(-11.22, -29.82) * mm, "end": v(-11.22, -28.69) * mm});
            skPoint(sketch, "E394.middle", {"position": v(-10.66, -29.25) * mm});
            skLineSegment(sketch, "E395.bottom", {"start": v(-7.48, -29.82) * mm, "end": v(-8.6, -29.82) * mm});
            skLineSegment(sketch, "E395.top", {"start": v(-7.48, -28.69) * mm, "end": v(-8.6, -28.69) * mm});
            skLineSegment(sketch, "E395.left", {"start": v(-7.48, -29.82) * mm, "end": v(-7.48, -28.69) * mm});
            skLineSegment(sketch, "E395.right", {"start": v(-8.6, -29.82) * mm, "end": v(-8.6, -28.69) * mm});
            skPoint(sketch, "E395.middle", {"position": v(-8.05, -29.25) * mm});
            skLineSegment(sketch, "E396.bottom", {"start": v(-4.93, -29.82) * mm, "end": v(-6.06, -29.82) * mm});
            skLineSegment(sketch, "E396.top", {"start": v(-4.93, -28.69) * mm, "end": v(-6.06, -28.69) * mm});
            skLineSegment(sketch, "E396.left", {"start": v(-4.93, -29.82) * mm, "end": v(-4.93, -28.69) * mm});
            skLineSegment(sketch, "E396.right", {"start": v(-6.06, -29.82) * mm, "end": v(-6.06, -28.69) * mm});
            skPoint(sketch, "E396.middle", {"position": v(-5.5, -29.25) * mm});
            skLineSegment(sketch, "E397.bottom", {"start": v(-2.48, -29.82) * mm, "end": v(-3.63, -29.82) * mm});
            skLineSegment(sketch, "E397.top", {"start": v(-2.48, -28.68) * mm, "end": v(-3.63, -28.68) * mm});
            skLineSegment(sketch, "E397.left", {"start": v(-2.48, -29.82) * mm, "end": v(-2.48, -28.68) * mm});
            skLineSegment(sketch, "E397.right", {"start": v(-3.63, -29.82) * mm, "end": v(-3.63, -28.68) * mm});
            skPoint(sketch, "E397.middle", {"position": v(-3.05, -29.25) * mm});
            skLineSegment(sketch, "E398.bottom", {"start": v(-0.05, -29.82) * mm, "end": v(-1.2, -29.82) * mm});
            skLineSegment(sketch, "E398.top", {"start": v(-0.05, -28.68) * mm, "end": v(-1.2, -28.68) * mm});
            skLineSegment(sketch, "E398.left", {"start": v(-0.05, -29.82) * mm, "end": v(-0.05, -28.68) * mm});
            skLineSegment(sketch, "E398.right", {"start": v(-1.2, -29.82) * mm, "end": v(-1.2, -28.68) * mm});
            skPoint(sketch, "E398.middle", {"position": v(-0.63, -29.25) * mm});
            skLineSegment(sketch, "E399.bottom", {"start": v(-17.98, -28.16) * mm, "end": v(-19.75, -28.16) * mm});
            skLineSegment(sketch, "E399.top", {"start": v(-17.98, -30.32) * mm, "end": v(-19.75, -30.32) * mm});
            skLineSegment(sketch, "E399.left", {"start": v(-17.98, -28.16) * mm, "end": v(-17.98, -30.32) * mm});
            skLineSegment(sketch, "E399.right", {"start": v(-19.75, -28.16) * mm, "end": v(-19.75, -30.32) * mm});
            skLineSegment(sketch, "E400", {"start": v(-15.38, -28.68) * mm, "end": v(-15.38, -28.16) * mm});
            skLineSegment(sketch, "E401", {"start": v(-15.38, -28.16) * mm, "end": v(-17.04, -28.16) * mm});
            skLineSegment(sketch, "E402", {"start": v(-15.38, -29.83) * mm, "end": v(-15.38, -30.34) * mm});
            skLineSegment(sketch, "E403", {"start": v(-15.38, -30.34) * mm, "end": v(-17.04, -30.34) * mm});
            skLineSegment(sketch, "E404", {"start": v(-12.7, -28.69) * mm, "end": v(-12.7, -28.18) * mm});
            skLineSegment(sketch, "E405", {"start": v(-12.7, -28.18) * mm, "end": v(-14.35, -28.18) * mm});
            skLineSegment(sketch, "E406", {"start": v(-14.35, -28.18) * mm, "end": v(-14.35, -30.33) * mm});
            skLineSegment(sketch, "E407", {"start": v(-14.35, -30.33) * mm, "end": v(-12.7, -30.33) * mm});
            skLineSegment(sketch, "E408", {"start": v(-12.7, -30.33) * mm, "end": v(-12.7, -29.82) * mm});
            skLineSegment(sketch, "E409", {"start": v(-10.1, -28.69) * mm, "end": v(-10.1, -28.18) * mm});
            skLineSegment(sketch, "E410", {"start": v(-10.1, -28.18) * mm, "end": v(-11.75, -28.18) * mm});
            skLineSegment(sketch, "E411", {"start": v(-11.75, -28.18) * mm, "end": v(-11.75, -30.33) * mm});
            skLineSegment(sketch, "E412", {"start": v(-11.75, -30.33) * mm, "end": v(-10.1, -30.33) * mm});
            skLineSegment(sketch, "E413", {"start": v(-10.1, -30.33) * mm, "end": v(-10.1, -29.82) * mm});
            skLineSegment(sketch, "E414", {"start": v(-7.48, -28.69) * mm, "end": v(-7.48, -28.18) * mm});
            skLineSegment(sketch, "E415", {"start": v(-7.48, -28.18) * mm, "end": v(-9.14, -28.18) * mm});
            skLineSegment(sketch, "E416", {"start": v(-9.14, -28.18) * mm, "end": v(-9.14, -30.33) * mm});
            skLineSegment(sketch, "E417", {"start": v(-9.14, -30.33) * mm, "end": v(-7.48, -30.33) * mm});
            skLineSegment(sketch, "E418", {"start": v(-7.48, -30.33) * mm, "end": v(-7.48, -29.82) * mm});
            skLineSegment(sketch, "E419", {"start": v(-4.93, -28.69) * mm, "end": v(-4.93, -28.16) * mm});
            skLineSegment(sketch, "E420", {"start": v(-4.93, -28.16) * mm, "end": v(-6.6, -28.16) * mm});
            skLineSegment(sketch, "E421", {"start": v(-6.6, -28.16) * mm, "end": v(-6.6, -30.33) * mm});
            skLineSegment(sketch, "E422", {"start": v(-6.6, -30.33) * mm, "end": v(-4.93, -30.33) * mm});
            skLineSegment(sketch, "E423", {"start": v(-4.93, -30.33) * mm, "end": v(-4.93, -29.82) * mm});
            skLineSegment(sketch, "E424", {"start": v(-2.48, -28.68) * mm, "end": v(-2.48, -28.16) * mm});
            skLineSegment(sketch, "E425", {"start": v(-2.48, -28.16) * mm, "end": v(-4.12, -28.16) * mm});
            skLineSegment(sketch, "E426", {"start": v(-4.12, -28.16) * mm, "end": v(-4.12, -30.33) * mm});
            skLineSegment(sketch, "E427", {"start": v(-4.12, -30.33) * mm, "end": v(-2.48, -30.33) * mm});
            skLineSegment(sketch, "E428", {"start": v(-2.48, -30.33) * mm, "end": v(-2.48, -29.82) * mm});
            skLineSegment(sketch, "E429", {"start": v(-0.05, -28.68) * mm, "end": v(-0.05, -28.18) * mm});
            skLineSegment(sketch, "E430", {"start": v(-0.05, -28.18) * mm, "end": v(-1.7, -28.18) * mm});
            skLineSegment(sketch, "E431", {"start": v(-1.7, -28.18) * mm, "end": v(-1.7, -30.33) * mm});
            skLineSegment(sketch, "E432", {"start": v(-1.7, -30.33) * mm, "end": v(-0.05, -30.33) * mm});
            skLineSegment(sketch, "E433", {"start": v(-0.05, -30.33) * mm, "end": v(-0.05, -29.82) * mm});
            skLineSegment(sketch, "E434.bottom", {"start": v(2.47, -29.82) * mm, "end": v(1.32, -29.82) * mm});
            skLineSegment(sketch, "E434.top", {"start": v(2.47, -28.69) * mm, "end": v(1.32, -28.69) * mm});
            skLineSegment(sketch, "E434.left", {"start": v(2.47, -29.82) * mm, "end": v(2.47, -28.69) * mm});
            skLineSegment(sketch, "E434.right", {"start": v(1.32, -29.82) * mm, "end": v(1.32, -28.69) * mm});
            skPoint(sketch, "E434.middle", {"position": v(1.9, -29.25) * mm});
            skPoint(sketch, "E435.middle", {"position": v(4.45, -29.25) * mm});
            skLineSegment(sketch, "E436.bottom", {"start": v(5.02, -29.83) * mm, "end": v(3.87, -29.83) * mm});
            skLineSegment(sketch, "E436.top", {"start": v(5.02, -28.68) * mm, "end": v(3.87, -28.68) * mm});
            skLineSegment(sketch, "E436.left", {"start": v(5.02, -29.83) * mm, "end": v(5.02, -28.68) * mm});
            skLineSegment(sketch, "E436.right", {"start": v(3.87, -29.83) * mm, "end": v(3.87, -28.68) * mm});
            skLineSegment(sketch, "E437.bottom", {"start": v(7.53, -29.83) * mm, "end": v(6.39, -29.83) * mm});
            skLineSegment(sketch, "E437.top", {"start": v(7.53, -28.68) * mm, "end": v(6.39, -28.68) * mm});
            skLineSegment(sketch, "E437.left", {"start": v(7.53, -29.83) * mm, "end": v(7.53, -28.68) * mm});
            skLineSegment(sketch, "E437.right", {"start": v(6.39, -29.83) * mm, "end": v(6.39, -28.68) * mm});
            skPoint(sketch, "E437.middle", {"position": v(6.96, -29.25) * mm});
            skLineSegment(sketch, "E438.bottom", {"start": v(10.07, -29.83) * mm, "end": v(8.92, -29.83) * mm});
            skLineSegment(sketch, "E438.top", {"start": v(10.07, -28.68) * mm, "end": v(8.92, -28.68) * mm});
            skLineSegment(sketch, "E438.left", {"start": v(10.07, -29.83) * mm, "end": v(10.07, -28.68) * mm});
            skLineSegment(sketch, "E438.right", {"start": v(8.92, -29.83) * mm, "end": v(8.92, -28.68) * mm});
            skPoint(sketch, "E438.middle", {"position": v(9.5, -29.25) * mm});
            skLineSegment(sketch, "E439.bottom", {"start": v(12.6, -29.83) * mm, "end": v(11.45, -29.83) * mm});
            skLineSegment(sketch, "E439.top", {"start": v(12.6, -28.68) * mm, "end": v(11.45, -28.68) * mm});
            skLineSegment(sketch, "E439.left", {"start": v(12.6, -29.83) * mm, "end": v(12.6, -28.68) * mm});
            skLineSegment(sketch, "E439.right", {"start": v(11.45, -29.83) * mm, "end": v(11.45, -28.68) * mm});
            skPoint(sketch, "E439.middle", {"position": v(12.02, -29.25) * mm});
            skLineSegment(sketch, "E440.bottom", {"start": v(15.12, -29.83) * mm, "end": v(13.99, -29.83) * mm});
            skLineSegment(sketch, "E440.top", {"start": v(15.12, -28.68) * mm, "end": v(13.99, -28.68) * mm});
            skLineSegment(sketch, "E440.left", {"start": v(15.12, -29.83) * mm, "end": v(15.12, -28.68) * mm});
            skLineSegment(sketch, "E440.right", {"start": v(13.99, -29.83) * mm, "end": v(13.99, -28.68) * mm});
            skPoint(sketch, "E440.middle", {"position": v(14.56, -29.25) * mm});
            skLineSegment(sketch, "E441.bottom", {"start": v(21.03, -29.83) * mm, "end": v(19.9, -29.83) * mm});
            skLineSegment(sketch, "E441.top", {"start": v(21.03, -28.68) * mm, "end": v(19.9, -28.68) * mm});
            skLineSegment(sketch, "E441.left", {"start": v(21.03, -29.83) * mm, "end": v(21.03, -28.68) * mm});
            skLineSegment(sketch, "E441.right", {"start": v(19.9, -29.83) * mm, "end": v(19.9, -28.68) * mm});
            skPoint(sketch, "E441.middle", {"position": v(20.46, -29.25) * mm});
            skLineSegment(sketch, "E442.bottom", {"start": v(23.56, -29.83) * mm, "end": v(22.42, -29.83) * mm});
            skLineSegment(sketch, "E442.top", {"start": v(23.56, -28.68) * mm, "end": v(22.42, -28.68) * mm});
            skLineSegment(sketch, "E442.left", {"start": v(23.56, -29.83) * mm, "end": v(23.56, -28.68) * mm});
            skLineSegment(sketch, "E442.right", {"start": v(22.42, -29.83) * mm, "end": v(22.42, -28.68) * mm});
            skPoint(sketch, "E442.middle", {"position": v(23, -29.25) * mm});
            skPoint(sketch, "E443.middle", {"position": v(25.54, -29.25) * mm});
            skLineSegment(sketch, "E444.bottom", {"start": v(26.11, -29.82) * mm, "end": v(24.96, -29.82) * mm});
            skLineSegment(sketch, "E444.top", {"start": v(26.11, -28.68) * mm, "end": v(24.96, -28.68) * mm});
            skLineSegment(sketch, "E444.left", {"start": v(26.11, -29.82) * mm, "end": v(26.11, -28.68) * mm});
            skLineSegment(sketch, "E444.right", {"start": v(24.96, -29.82) * mm, "end": v(24.96, -28.68) * mm});
            skLineSegment(sketch, "E445", {"start": v(2.47, -28.69) * mm, "end": v(2.47, -28.17) * mm});
            skLineSegment(sketch, "E446", {"start": v(2.47, -28.17) * mm, "end": v(0.82, -28.17) * mm});
            skLineSegment(sketch, "E447", {"start": v(0.82, -28.17) * mm, "end": v(0.82, -30.33) * mm});
            skLineSegment(sketch, "E448", {"start": v(0.82, -30.33) * mm, "end": v(2.47, -30.33) * mm});
            skLineSegment(sketch, "E449", {"start": v(2.47, -30.33) * mm, "end": v(2.47, -29.82) * mm});
            skLineSegment(sketch, "E450", {"start": v(5.02, -28.68) * mm, "end": v(5.02, -28.17) * mm});
            skLineSegment(sketch, "E451", {"start": v(5.02, -28.17) * mm, "end": v(3.37, -28.17) * mm});
            skLineSegment(sketch, "E452", {"start": v(3.37, -28.17) * mm, "end": v(3.37, -30.33) * mm});
            skLineSegment(sketch, "E453", {"start": v(3.37, -30.33) * mm, "end": v(5.02, -30.33) * mm});
            skLineSegment(sketch, "E454", {"start": v(5.02, -30.33) * mm, "end": v(5.02, -29.83) * mm});
            skLineSegment(sketch, "E455", {"start": v(7.53, -28.68) * mm, "end": v(7.53, -28.17) * mm});
            skLineSegment(sketch, "E456", {"start": v(7.53, -28.17) * mm, "end": v(5.88, -28.17) * mm});
            skLineSegment(sketch, "E457", {"start": v(5.88, -28.17) * mm, "end": v(5.88, -30.33) * mm});
            skLineSegment(sketch, "E458", {"start": v(5.88, -30.33) * mm, "end": v(7.53, -30.33) * mm});
            skLineSegment(sketch, "E459", {"start": v(7.53, -30.33) * mm, "end": v(7.53, -29.83) * mm});
            skLineSegment(sketch, "E460", {"start": v(10.07, -28.68) * mm, "end": v(10.07, -28.16) * mm});
            skLineSegment(sketch, "E461", {"start": v(10.07, -28.16) * mm, "end": v(8.41, -28.16) * mm});
            skLineSegment(sketch, "E462", {"start": v(8.41, -28.16) * mm, "end": v(8.43, -30.31) * mm});
            skLineSegment(sketch, "E463", {"start": v(8.43, -30.31) * mm, "end": v(10.07, -30.31) * mm});
            skLineSegment(sketch, "E464", {"start": v(10.07, -30.31) * mm, "end": v(10.07, -29.83) * mm});
            skLineSegment(sketch, "E465", {"start": v(12.6, -28.68) * mm, "end": v(12.6, -28.17) * mm});
            skLineSegment(sketch, "E466", {"start": v(12.6, -28.17) * mm, "end": v(10.95, -28.17) * mm});
            skLineSegment(sketch, "E467", {"start": v(10.95, -28.17) * mm, "end": v(10.95, -30.32) * mm});
            skLineSegment(sketch, "E468", {"start": v(10.95, -30.32) * mm, "end": v(12.6, -30.32) * mm});
            skLineSegment(sketch, "E469", {"start": v(12.6, -30.32) * mm, "end": v(12.6, -29.83) * mm});
            skLineSegment(sketch, "E470", {"start": v(15.12, -28.68) * mm, "end": v(15.12, -28.18) * mm});
            skLineSegment(sketch, "E471", {"start": v(15.12, -28.18) * mm, "end": v(13.48, -28.18) * mm});
            skLineSegment(sketch, "E472", {"start": v(13.48, -28.18) * mm, "end": v(13.48, -30.34) * mm});
            skLineSegment(sketch, "E473", {"start": v(13.48, -30.34) * mm, "end": v(15.12, -30.34) * mm});
            skLineSegment(sketch, "E474", {"start": v(15.12, -30.34) * mm, "end": v(15.12, -29.83) * mm});
            skLineSegment(sketch, "E475", {"start": v(21.03, -28.68) * mm, "end": v(21.03, -28.17) * mm});
            skLineSegment(sketch, "E476", {"start": v(21.03, -28.17) * mm, "end": v(19.38, -28.17) * mm});
            skLineSegment(sketch, "E477", {"start": v(19.38, -28.17) * mm, "end": v(19.38, -30.32) * mm});
            skLineSegment(sketch, "E478", {"start": v(19.38, -30.32) * mm, "end": v(21.03, -30.32) * mm});
            skLineSegment(sketch, "E479", {"start": v(21.03, -30.32) * mm, "end": v(21.03, -29.83) * mm});
            skLineSegment(sketch, "E480", {"start": v(23.56, -28.68) * mm, "end": v(23.56, -28.17) * mm});
            skLineSegment(sketch, "E481", {"start": v(23.56, -28.17) * mm, "end": v(21.92, -28.17) * mm});
            skLineSegment(sketch, "E482", {"start": v(21.92, -28.17) * mm, "end": v(21.92, -30.32) * mm});
            skLineSegment(sketch, "E483", {"start": v(21.92, -30.32) * mm, "end": v(23.56, -30.32) * mm});
            skLineSegment(sketch, "E484", {"start": v(23.56, -30.32) * mm, "end": v(23.56, -29.83) * mm});
            skLineSegment(sketch, "E485", {"start": v(26.11, -28.68) * mm, "end": v(26.11, -28.18) * mm});
            skLineSegment(sketch, "E486", {"start": v(26.11, -28.18) * mm, "end": v(24.46, -28.18) * mm});
            skLineSegment(sketch, "E487", {"start": v(24.46, -28.18) * mm, "end": v(24.46, -30.33) * mm});
            skLineSegment(sketch, "E488", {"start": v(24.46, -30.33) * mm, "end": v(26.11, -30.33) * mm});
            skLineSegment(sketch, "E489", {"start": v(26.11, -30.33) * mm, "end": v(26.11, -29.82) * mm});
            skLineSegment(sketch, "E490.bottom", {"start": v(23.57, 10.64) * mm, "end": v(22.42, 10.64) * mm});
            skLineSegment(sketch, "E490.top", {"start": v(23.57, 11.77) * mm, "end": v(22.42, 11.77) * mm});
            skLineSegment(sketch, "E490.left", {"start": v(23.57, 10.64) * mm, "end": v(23.57, 11.77) * mm});
            skLineSegment(sketch, "E490.right", {"start": v(22.42, 10.64) * mm, "end": v(22.42, 11.77) * mm});
            skPoint(sketch, "E490.middle", {"position": v(23, 11.2) * mm});
            skLineSegment(sketch, "E491.bottom", {"start": v(21.03, 10.64) * mm, "end": v(19.9, 10.64) * mm});
            skLineSegment(sketch, "E491.top", {"start": v(21.03, 11.77) * mm, "end": v(19.9, 11.77) * mm});
            skLineSegment(sketch, "E491.left", {"start": v(21.03, 10.64) * mm, "end": v(21.03, 11.77) * mm});
            skLineSegment(sketch, "E491.right", {"start": v(19.9, 10.64) * mm, "end": v(19.9, 11.77) * mm});
            skPoint(sketch, "E491.middle", {"position": v(20.46, 11.2) * mm});
            skLineSegment(sketch, "E492.bottom", {"start": v(15.13, 10.64) * mm, "end": v(13.98, 10.64) * mm});
            skLineSegment(sketch, "E492.top", {"start": v(15.13, 11.77) * mm, "end": v(13.98, 11.77) * mm});
            skLineSegment(sketch, "E492.left", {"start": v(15.13, 10.64) * mm, "end": v(15.13, 11.77) * mm});
            skLineSegment(sketch, "E492.right", {"start": v(13.98, 10.64) * mm, "end": v(13.98, 11.77) * mm});
            skPoint(sketch, "E492.middle", {"position": v(14.56, 11.2) * mm});
            skLineSegment(sketch, "E493.bottom", {"start": v(12.6, 10.64) * mm, "end": v(11.45, 10.64) * mm});
            skLineSegment(sketch, "E493.top", {"start": v(12.6, 11.78) * mm, "end": v(11.45, 11.78) * mm});
            skLineSegment(sketch, "E493.left", {"start": v(12.6, 10.64) * mm, "end": v(12.6, 11.78) * mm});
            skLineSegment(sketch, "E493.right", {"start": v(11.45, 10.64) * mm, "end": v(11.45, 11.78) * mm});
            skPoint(sketch, "E493.middle", {"position": v(12.02, 11.2) * mm});
            skLineSegment(sketch, "E494.bottom", {"start": v(10.07, 10.64) * mm, "end": v(8.92, 10.64) * mm});
            skLineSegment(sketch, "E494.top", {"start": v(10.07, 11.78) * mm, "end": v(8.92, 11.78) * mm});
            skLineSegment(sketch, "E494.left", {"start": v(10.07, 10.64) * mm, "end": v(10.07, 11.78) * mm});
            skLineSegment(sketch, "E494.right", {"start": v(8.92, 10.64) * mm, "end": v(8.92, 11.78) * mm});
            skPoint(sketch, "E494.middle", {"position": v(9.5, 11.2) * mm});
            skLineSegment(sketch, "E495.bottom", {"start": v(7.52, 10.64) * mm, "end": v(6.4, 10.64) * mm});
            skLineSegment(sketch, "E495.top", {"start": v(7.52, 11.78) * mm, "end": v(6.4, 11.78) * mm});
            skLineSegment(sketch, "E495.left", {"start": v(7.52, 10.64) * mm, "end": v(7.52, 11.78) * mm});
            skLineSegment(sketch, "E495.right", {"start": v(6.4, 10.64) * mm, "end": v(6.4, 11.78) * mm});
            skPoint(sketch, "E495.middle", {"position": v(6.96, 11.2) * mm});
            skLineSegment(sketch, "E496.bottom", {"start": v(5.01, 10.64) * mm, "end": v(3.88, 10.64) * mm});
            skLineSegment(sketch, "E496.top", {"start": v(5.01, 11.78) * mm, "end": v(3.88, 11.78) * mm});
            skLineSegment(sketch, "E496.left", {"start": v(5.01, 10.64) * mm, "end": v(5.01, 11.78) * mm});
            skLineSegment(sketch, "E496.right", {"start": v(3.88, 10.64) * mm, "end": v(3.88, 11.78) * mm});
            skPoint(sketch, "E496.middle", {"position": v(4.45, 11.2) * mm});
            skLineSegment(sketch, "E497.bottom", {"start": v(2.46, 10.64) * mm, "end": v(1.33, 10.64) * mm});
            skLineSegment(sketch, "E497.top", {"start": v(2.46, 11.78) * mm, "end": v(1.33, 11.78) * mm});
            skLineSegment(sketch, "E497.left", {"start": v(2.46, 10.64) * mm, "end": v(2.46, 11.78) * mm});
            skLineSegment(sketch, "E497.right", {"start": v(1.33, 10.64) * mm, "end": v(1.33, 11.78) * mm});
            skPoint(sketch, "E497.middle", {"position": v(1.9, 11.2) * mm});
            skLineSegment(sketch, "E498.bottom", {"start": v(-0.05, 10.64) * mm, "end": v(-1.2, 10.64) * mm});
            skLineSegment(sketch, "E498.top", {"start": v(-0.05, 11.77) * mm, "end": v(-1.2, 11.77) * mm});
            skLineSegment(sketch, "E498.left", {"start": v(-0.05, 10.64) * mm, "end": v(-0.05, 11.77) * mm});
            skLineSegment(sketch, "E498.right", {"start": v(-1.2, 10.64) * mm, "end": v(-1.2, 11.77) * mm});
            skPoint(sketch, "E498.middle", {"position": v(-0.63, 11.2) * mm});
            skLineSegment(sketch, "E499.bottom", {"start": v(-2.48, 10.63) * mm, "end": v(-3.62, 10.63) * mm});
            skLineSegment(sketch, "E499.top", {"start": v(-2.48, 11.78) * mm, "end": v(-3.62, 11.78) * mm});
            skLineSegment(sketch, "E499.left", {"start": v(-2.48, 10.63) * mm, "end": v(-2.48, 11.78) * mm});
            skLineSegment(sketch, "E499.right", {"start": v(-3.62, 10.63) * mm, "end": v(-3.62, 11.78) * mm});
            skPoint(sketch, "E499.middle", {"position": v(-3.05, 11.2) * mm});
            skLineSegment(sketch, "E500.bottom", {"start": v(-4.92, 10.64) * mm, "end": v(-6.07, 10.64) * mm});
            skLineSegment(sketch, "E500.top", {"start": v(-4.92, 11.78) * mm, "end": v(-6.07, 11.78) * mm});
            skLineSegment(sketch, "E500.left", {"start": v(-4.92, 10.64) * mm, "end": v(-4.92, 11.78) * mm});
            skLineSegment(sketch, "E500.right", {"start": v(-6.07, 10.64) * mm, "end": v(-6.07, 11.78) * mm});
            skPoint(sketch, "E500.middle", {"position": v(-5.5, 11.2) * mm});
            skLineSegment(sketch, "E501.bottom", {"start": v(-7.48, 10.64) * mm, "end": v(-8.61, 10.64) * mm});
            skLineSegment(sketch, "E501.top", {"start": v(-7.48, 11.78) * mm, "end": v(-8.61, 11.78) * mm});
            skLineSegment(sketch, "E501.left", {"start": v(-7.48, 10.64) * mm, "end": v(-7.48, 11.78) * mm});
            skLineSegment(sketch, "E501.right", {"start": v(-8.61, 10.64) * mm, "end": v(-8.61, 11.78) * mm});
            skPoint(sketch, "E501.middle", {"position": v(-8.05, 11.2) * mm});
            skLineSegment(sketch, "E502.bottom", {"start": v(-10.08, 10.63) * mm, "end": v(-11.24, 10.63) * mm});
            skLineSegment(sketch, "E502.top", {"start": v(-10.08, 11.78) * mm, "end": v(-11.24, 11.78) * mm});
            skLineSegment(sketch, "E502.left", {"start": v(-10.08, 10.63) * mm, "end": v(-10.08, 11.78) * mm});
            skLineSegment(sketch, "E502.right", {"start": v(-11.24, 10.63) * mm, "end": v(-11.24, 11.78) * mm});
            skPoint(sketch, "E502.middle", {"position": v(-10.66, 11.2) * mm});
            skLineSegment(sketch, "E503.bottom", {"start": v(-12.7, 10.64) * mm, "end": v(-13.86, 10.64) * mm});
            skLineSegment(sketch, "E503.top", {"start": v(-12.7, 11.78) * mm, "end": v(-13.86, 11.78) * mm});
            skLineSegment(sketch, "E503.left", {"start": v(-12.7, 10.64) * mm, "end": v(-12.7, 11.78) * mm});
            skLineSegment(sketch, "E503.right", {"start": v(-13.86, 10.64) * mm, "end": v(-13.86, 11.78) * mm});
            skPoint(sketch, "E503.middle", {"position": v(-13.28, 11.2) * mm});
            skLineSegment(sketch, "E504.bottom", {"start": v(-15.4, 10.64) * mm, "end": v(-16.53, 10.64) * mm});
            skLineSegment(sketch, "E504.top", {"start": v(-15.4, 11.78) * mm, "end": v(-16.53, 11.78) * mm});
            skLineSegment(sketch, "E504.left", {"start": v(-15.4, 10.64) * mm, "end": v(-15.4, 11.78) * mm});
            skLineSegment(sketch, "E504.right", {"start": v(-16.53, 10.64) * mm, "end": v(-16.53, 11.78) * mm});
            skPoint(sketch, "E504.middle", {"position": v(-15.96, 11.2) * mm});
            skLineSegment(sketch, "E505.bottom", {"start": v(26.1, 10.64) * mm, "end": v(24.97, 10.64) * mm});
            skLineSegment(sketch, "E505.top", {"start": v(26.1, 11.78) * mm, "end": v(24.97, 11.78) * mm});
            skLineSegment(sketch, "E505.left", {"start": v(26.1, 10.64) * mm, "end": v(26.1, 11.78) * mm});
            skLineSegment(sketch, "E505.right", {"start": v(24.97, 10.64) * mm, "end": v(24.97, 11.78) * mm});
            skPoint(sketch, "E505.middle", {"position": v(25.54, 11.2) * mm});
            skLineSegment(sketch, "E506", {"start": v(26.1, 11.78) * mm, "end": v(26.1, 12.28) * mm});
            skLineSegment(sketch, "E507", {"start": v(26.1, 12.28) * mm, "end": v(24.46, 12.28) * mm});
            skLineSegment(sketch, "E508", {"start": v(24.46, 12.28) * mm, "end": v(24.46, 10.11) * mm});
            skLineSegment(sketch, "E509", {"start": v(24.46, 10.11) * mm, "end": v(26.1, 10.11) * mm});
            skLineSegment(sketch, "E510", {"start": v(26.1, 10.11) * mm, "end": v(26.1, 10.64) * mm});
            skLineSegment(sketch, "E511.bottom", {"start": v(-17.99, 10.64) * mm, "end": v(-19.13, 10.64) * mm});
            skLineSegment(sketch, "E511.top", {"start": v(-17.99, 11.78) * mm, "end": v(-19.13, 11.78) * mm});
            skLineSegment(sketch, "E511.left", {"start": v(-17.99, 10.64) * mm, "end": v(-17.99, 11.78) * mm});
            skLineSegment(sketch, "E511.right", {"start": v(-19.13, 10.64) * mm, "end": v(-19.13, 11.78) * mm});
            skPoint(sketch, "E511.middle", {"position": v(-18.56, 11.2) * mm});
            skLineSegment(sketch, "E512", {"start": v(-17.99, 11.78) * mm, "end": v(-17.99, 12.28) * mm});
            skLineSegment(sketch, "E513", {"start": v(-17.99, 12.28) * mm, "end": v(-19.64, 12.28) * mm});
            skLineSegment(sketch, "E514", {"start": v(-19.64, 12.28) * mm, "end": v(-19.64, 10.12) * mm});
            skLineSegment(sketch, "E515", {"start": v(-19.64, 10.12) * mm, "end": v(-17.99, 10.12) * mm});
            skLineSegment(sketch, "E516", {"start": v(-17.99, 10.12) * mm, "end": v(-17.99, 10.64) * mm});
            skLineSegment(sketch, "E517", {"start": v(-15.4, 11.78) * mm, "end": v(-15.4, 12.28) * mm});
            skLineSegment(sketch, "E518", {"start": v(-15.4, 12.28) * mm, "end": v(-17.04, 12.28) * mm});
            skLineSegment(sketch, "E519", {"start": v(-17.04, 12.28) * mm, "end": v(-17.04, 10.12) * mm});
            skLineSegment(sketch, "E520", {"start": v(-17.04, 10.12) * mm, "end": v(-15.4, 10.12) * mm});
            skLineSegment(sketch, "E521", {"start": v(-15.4, 10.12) * mm, "end": v(-15.4, 10.64) * mm});
            skLineSegment(sketch, "E522", {"start": v(-12.7, 11.78) * mm, "end": v(-12.7, 12.28) * mm});
            skLineSegment(sketch, "E523", {"start": v(-12.7, 12.28) * mm, "end": v(-14.36, 12.28) * mm});
            skLineSegment(sketch, "E524", {"start": v(-14.36, 12.28) * mm, "end": v(-14.36, 10.12) * mm});
            skLineSegment(sketch, "E525", {"start": v(-14.36, 10.12) * mm, "end": v(-12.7, 10.12) * mm});
            skLineSegment(sketch, "E526", {"start": v(-12.7, 10.12) * mm, "end": v(-12.7, 10.64) * mm});
            skLineSegment(sketch, "E527", {"start": v(-10.08, 11.78) * mm, "end": v(-10.08, 12.28) * mm});
            skLineSegment(sketch, "E528", {"start": v(-10.08, 12.28) * mm, "end": v(-11.73, 12.28) * mm});
            skLineSegment(sketch, "E529", {"start": v(-11.73, 12.28) * mm, "end": v(-11.73, 10.12) * mm});
            skLineSegment(sketch, "E530", {"start": v(-11.73, 10.12) * mm, "end": v(-10.08, 10.12) * mm});
            skLineSegment(sketch, "E531", {"start": v(-10.08, 10.12) * mm, "end": v(-10.08, 10.63) * mm});
            skLineSegment(sketch, "E532", {"start": v(-7.48, 11.78) * mm, "end": v(-7.48, 12.28) * mm});
            skLineSegment(sketch, "E533", {"start": v(-7.48, 12.28) * mm, "end": v(-9.13, 12.28) * mm});
            skLineSegment(sketch, "E534", {"start": v(-9.13, 12.28) * mm, "end": v(-9.13, 10.12) * mm});
            skLineSegment(sketch, "E535", {"start": v(-9.13, 10.12) * mm, "end": v(-7.48, 10.12) * mm});
            skLineSegment(sketch, "E536", {"start": v(-7.48, 10.12) * mm, "end": v(-7.48, 10.64) * mm});
            skLineSegment(sketch, "E537", {"start": v(-4.92, 11.78) * mm, "end": v(-4.92, 12.28) * mm});
            skLineSegment(sketch, "E538", {"start": v(-4.92, 12.28) * mm, "end": v(-6.56, 12.28) * mm});
            skLineSegment(sketch, "E539", {"start": v(-6.56, 12.28) * mm, "end": v(-6.56, 10.12) * mm});
            skLineSegment(sketch, "E540", {"start": v(-6.56, 10.12) * mm, "end": v(-4.92, 10.12) * mm});
            skLineSegment(sketch, "E541", {"start": v(-4.92, 10.12) * mm, "end": v(-4.92, 10.64) * mm});
            skLineSegment(sketch, "E542", {"start": v(-2.48, 11.78) * mm, "end": v(-2.48, 12.3) * mm});
            skLineSegment(sketch, "E543", {"start": v(-2.48, 12.3) * mm, "end": v(-4.12, 12.3) * mm});
            skLineSegment(sketch, "E544", {"start": v(-4.12, 12.3) * mm, "end": v(-4.12, 10.15) * mm});
            skLineSegment(sketch, "E545", {"start": v(-4.12, 10.15) * mm, "end": v(-2.48, 10.15) * mm});
            skLineSegment(sketch, "E546", {"start": v(-2.48, 10.15) * mm, "end": v(-2.48, 10.63) * mm});
            skLineSegment(sketch, "E547", {"start": v(-0.05, 11.77) * mm, "end": v(-0.05, 12.28) * mm});
            skLineSegment(sketch, "E548", {"start": v(-0.05, 12.28) * mm, "end": v(-1.7, 12.28) * mm});
            skLineSegment(sketch, "E549", {"start": v(-1.7, 12.28) * mm, "end": v(-1.7, 10.13) * mm});
            skLineSegment(sketch, "E550", {"start": v(-1.7, 10.13) * mm, "end": v(-0.05, 10.13) * mm});
            skLineSegment(sketch, "E551", {"start": v(-0.05, 10.13) * mm, "end": v(-0.05, 10.64) * mm});
            skLineSegment(sketch, "E552", {"start": v(2.46, 11.78) * mm, "end": v(2.46, 12.3) * mm});
            skLineSegment(sketch, "E553", {"start": v(2.46, 12.3) * mm, "end": v(0.82, 12.3) * mm});
            skLineSegment(sketch, "E554", {"start": v(0.82, 12.3) * mm, "end": v(0.82, 10.13) * mm});
            skLineSegment(sketch, "E555", {"start": v(0.82, 10.13) * mm, "end": v(2.46, 10.13) * mm});
            skLineSegment(sketch, "E556", {"start": v(2.46, 10.13) * mm, "end": v(2.46, 10.64) * mm});
            skLineSegment(sketch, "E557", {"start": v(5.01, 11.78) * mm, "end": v(5.01, 12.3) * mm});
            skLineSegment(sketch, "E558", {"start": v(5.01, 12.3) * mm, "end": v(3.37, 12.3) * mm});
            skLineSegment(sketch, "E559", {"start": v(3.37, 12.3) * mm, "end": v(3.37, 10.13) * mm});
            skLineSegment(sketch, "E560", {"start": v(3.37, 10.13) * mm, "end": v(5.01, 10.13) * mm});
            skLineSegment(sketch, "E561", {"start": v(5.01, 10.13) * mm, "end": v(5.01, 10.64) * mm});
            skLineSegment(sketch, "E562", {"start": v(7.52, 11.78) * mm, "end": v(7.52, 12.3) * mm});
            skLineSegment(sketch, "E563", {"start": v(7.52, 12.3) * mm, "end": v(5.87, 12.3) * mm});
            skLineSegment(sketch, "E564", {"start": v(5.87, 12.3) * mm, "end": v(5.87, 10.13) * mm});
            skLineSegment(sketch, "E565", {"start": v(5.87, 10.13) * mm, "end": v(7.52, 10.13) * mm});
            skLineSegment(sketch, "E566", {"start": v(7.52, 10.13) * mm, "end": v(7.52, 10.64) * mm});
            skLineSegment(sketch, "E567", {"start": v(10.07, 11.78) * mm, "end": v(10.07, 12.3) * mm});
            skLineSegment(sketch, "E568", {"start": v(10.07, 12.3) * mm, "end": v(8.42, 12.3) * mm});
            skLineSegment(sketch, "E569", {"start": v(8.42, 12.3) * mm, "end": v(8.42, 10.13) * mm});
            skLineSegment(sketch, "E570", {"start": v(8.42, 10.13) * mm, "end": v(10.07, 10.13) * mm});
            skLineSegment(sketch, "E571", {"start": v(10.07, 10.13) * mm, "end": v(10.07, 10.64) * mm});
            skLineSegment(sketch, "E572", {"start": v(12.6, 11.78) * mm, "end": v(12.6, 12.3) * mm});
            skLineSegment(sketch, "E573", {"start": v(12.6, 12.3) * mm, "end": v(10.95, 12.3) * mm});
            skLineSegment(sketch, "E574", {"start": v(10.95, 12.3) * mm, "end": v(10.95, 10.13) * mm});
            skLineSegment(sketch, "E575", {"start": v(10.95, 10.13) * mm, "end": v(12.6, 10.13) * mm});
            skLineSegment(sketch, "E576", {"start": v(12.6, 10.13) * mm, "end": v(12.6, 10.64) * mm});
            skLineSegment(sketch, "E577", {"start": v(15.13, 11.77) * mm, "end": v(15.13, 12.3) * mm});
            skLineSegment(sketch, "E578", {"start": v(15.13, 12.3) * mm, "end": v(13.47, 12.3) * mm});
            skLineSegment(sketch, "E579", {"start": v(13.47, 12.3) * mm, "end": v(13.47, 10.13) * mm});
            skLineSegment(sketch, "E580", {"start": v(13.47, 10.13) * mm, "end": v(15.13, 10.13) * mm});
            skLineSegment(sketch, "E581", {"start": v(15.13, 10.13) * mm, "end": v(15.13, 10.64) * mm});
            skLineSegment(sketch, "E582", {"start": v(21.03, 11.77) * mm, "end": v(21.03, 12.3) * mm});
            skLineSegment(sketch, "E583", {"start": v(21.03, 12.3) * mm, "end": v(19.38, 12.3) * mm});
            skLineSegment(sketch, "E584", {"start": v(19.38, 12.3) * mm, "end": v(19.38, 10.13) * mm});
            skLineSegment(sketch, "E585", {"start": v(19.38, 10.13) * mm, "end": v(21.03, 10.13) * mm});
            skLineSegment(sketch, "E586", {"start": v(21.03, 10.13) * mm, "end": v(21.03, 10.64) * mm});
            skLineSegment(sketch, "E587", {"start": v(23.57, 11.77) * mm, "end": v(23.57, 12.3) * mm});
            skLineSegment(sketch, "E588", {"start": v(23.57, 12.3) * mm, "end": v(21.92, 12.3) * mm});
            skLineSegment(sketch, "E589", {"start": v(21.92, 12.3) * mm, "end": v(21.92, 10.13) * mm});
            skLineSegment(sketch, "E590", {"start": v(21.92, 10.13) * mm, "end": v(23.57, 10.13) * mm});
            skLineSegment(sketch, "E591", {"start": v(23.57, 10.13) * mm, "end": v(23.57, 10.64) * mm});
            skLineSegment(sketch, "E592.bottom", {"start": v(-26.46, -12.16) * mm, "end": v(-25.44, -12.16) * mm});
            skLineSegment(sketch, "E592.top", {"start": v(-26.46, -11.14) * mm, "end": v(-25.44, -11.14) * mm});
            skLineSegment(sketch, "E592.left", {"start": v(-26.46, -12.16) * mm, "end": v(-26.46, -11.14) * mm});
            skLineSegment(sketch, "E592.right", {"start": v(-25.44, -12.16) * mm, "end": v(-25.44, -11.14) * mm});
            skLineSegment(sketch, "E593", {"start": v(-24.56, -12.16) * mm, "end": v(-24.58, -10.47) * mm});
            skLineSegment(sketch, "E594", {"start": v(-27.3, -12.16) * mm, "end": v(-27.3, -10.47) * mm});
            skLineSegment(sketch, "E595", {"start": v(-27.3, -10.47) * mm, "end": v(-24.58, -10.47) * mm});
            skLineSegment(sketch, "E596", {"start": v(-24.56, -12.16) * mm, "end": v(-25.44, -12.16) * mm});
            skLineSegment(sketch, "E597", {"start": v(-26.46, -12.16) * mm, "end": v(-27.3, -12.16) * mm});
            skSolve(sketch);
        }
        {
            var Q0;
            Q0=makeQuery(id+"F0.imprint","IMPRINT",FACE,{"disambiguationData":[TD([[makeQuery(id+"F0.imprint","IMPRINT",EDGE,{"derivedFrom":sQuery(id+"F0.wireOp",EDGE,"E38.bottom")}),-1.0]])]});
            var Q1;
            Q1=makeQuery(id+"F0.imprint","IMPRINT",FACE,{"disambiguationData":[TD([[makeQuery(id+"F0.imprint","IMPRINT",EDGE,{"derivedFrom":sQuery(id+"F0.wireOp",EDGE,"E69.bottom")}),-1.0]])]});
            var Q2;
            Q2=makeQuery(id+"F0.imprint","IMPRINT",FACE,{"disambiguationData":[TD([[makeQuery(id+"F0.imprint","IMPRINT",EDGE,{"derivedFrom":sQuery(id+"F0.wireOp",EDGE,"RSuOeHIz-FbLd-ODKA-Awp0-7HqHRt6EF7fj")}),-1.0]])]});
            var Q3;
            Q3=makeQuery(id+"F0.imprint","IMPRINT",FACE,{"disambiguationData":[TD([[makeQuery(id+"F0.imprint","IMPRINT",EDGE,{"derivedFrom":sQuery(id+"F0.wireOp",EDGE,"E134")}),1.0]])]});
            var Q4;
            {var subQ0=sQuery(id+"F0.wireOp",EDGE,"OAMKzs4L-roZE-D8En-6iZY-EV7lWOimPANv");Q4=makeQuery(id+"F0.imprint","IMPRINT",FACE,{"disambiguationData":[TD([[makeQuery(id+"F0.imprint","IMPRINT",EDGE,{"derivedFrom":subQ0}),1.0]])]});}
            var Q5;
            {var subQ0=sQuery(id+"F0.wireOp",EDGE,"CW9L22bO-3VVT-gbfZ-IgyG-zfkkDui3gcl3");Q5=makeQuery(id+"F0.imprint","IMPRINT",FACE,{"disambiguationData":[TD([[makeQuery(id+"F0.imprint","IMPRINT",EDGE,{"derivedFrom":subQ0}),-1.0]])]});}
            var Q6;
            Q6=makeQuery(id+"F0.imprint","IMPRINT",FACE,{"disambiguationData":[TD([[makeQuery(id+"F0.imprint","IMPRINT",EDGE,{"derivedFrom":sQuery(id+"F0.wireOp",EDGE,"kevfQ62I-5Mcz-cfJ3-i68M-SCrzjStlXqoZ")}),-1.0]])]});
            var Q7;
            {var subQ3=sQuery(id+"F0.wireOp",EDGE,"E1.bottom");Q7=makeQuery(id+"F0.imprint","IMPRINT",FACE,{"disambiguationData":[TD([[makeQuery(id+"F0.imprint","IMPRINT",EDGE,{"derivedFrom":subQ3}),-1.0]])]});}
            var Q8;
            {var subQ3=sQuery(id+"F0.wireOp",EDGE,"E2.bottom");Q8=makeQuery(id+"F0.imprint","IMPRINT",FACE,{"disambiguationData":[TD([[makeQuery(id+"F0.imprint","IMPRINT",EDGE,{"derivedFrom":subQ3}),-1.0]])]});}
            var Q9;
            {var subQ3=sQuery(id+"F0.wireOp",EDGE,"E3.bottom");Q9=makeQuery(id+"F0.imprint","IMPRINT",FACE,{"disambiguationData":[TD([[makeQuery(id+"F0.imprint","IMPRINT",EDGE,{"derivedFrom":subQ3}),-1.0]])]});}
            var Q10;
            {var subQ3=sQuery(id+"F0.wireOp",EDGE,"E4.bottom");Q10=makeQuery(id+"F0.imprint","IMPRINT",FACE,{"disambiguationData":[TD([[makeQuery(id+"F0.imprint","IMPRINT",EDGE,{"derivedFrom":subQ3}),-1.0]])]});}
            var Q11;
            {var subQ0=sQuery(id+"F0.wireOp",EDGE,"qrdcftoR-PqJE-Aaip-Lt0B-KKN4o6upEuf8");Q11=makeQuery(id+"F0.imprint","IMPRINT",FACE,{"disambiguationData":[TD([[makeQuery(id+"F0.imprint","IMPRINT",EDGE,{"derivedFrom":subQ0}),-1.0]])]});}
            var Q12;
            {var subQ3=sQuery(id+"F0.wireOp",EDGE,"E68.bottom");Q12=makeQuery(id+"F0.imprint","IMPRINT",FACE,{"disambiguationData":[TD([[makeQuery(id+"F0.imprint","IMPRINT",EDGE,{"derivedFrom":subQ3}),-1.0]])]});}
            var Q13;
            Q13=makeQuery(id+"F0.imprint","IMPRINT",FACE,{"disambiguationData":[TD([[makeQuery(id+"F0.imprint","IMPRINT",EDGE,{"derivedFrom":sQuery(id+"F0.wireOp",EDGE,"E40.bottom")}),-1.0]])]});
            var Q14;
            Q14=makeQuery(id+"F0.imprint","IMPRINT",FACE,{"disambiguationData":[TD([[makeQuery(id+"F0.imprint","IMPRINT",EDGE,{"derivedFrom":sQuery(id+"F0.wireOp",EDGE,"E352")}),1.0]])]});
            var Q15;
            Q15=makeQuery(id+"F0.imprint","IMPRINT",FACE,{"disambiguationData":[TD([[makeQuery(id+"F0.imprint","IMPRINT",EDGE,{"derivedFrom":sQuery(id+"F0.wireOp",EDGE,"E302")}),1.0]])]});
            var Q16;
            {var subQ1=sQuery(id+"F0.wireOp",EDGE,"E39.bottom");Q16=makeQuery(id+"F0.imprint","IMPRINT",FACE,{"disambiguationData":[TD([[makeQuery(id+"F0.imprint","IMPRINT",EDGE,{"derivedFrom":subQ1}),-1.0]])]});}
            var Q17;
            Q17=makeQuery(id+"F0.imprint","IMPRINT",FACE,{"disambiguationData":[TD([[makeQuery(id+"F0.imprint","IMPRINT",EDGE,{"derivedFrom":sQuery(id+"F0.wireOp",EDGE,"E294")}),-1.0]])]});
            var Q18;
            {var subQ3=sQuery(id+"F0.wireOp",EDGE,"E43.bottom");Q18=makeQuery(id+"F0.imprint","IMPRINT",FACE,{"disambiguationData":[TD([[makeQuery(id+"F0.imprint","IMPRINT",EDGE,{"derivedFrom":subQ3}),-1.0]])]});}
            var Q19;
            Q19=makeQuery(id+"F0.imprint","IMPRINT",FACE,{"disambiguationData":[TD([[makeQuery(id+"F0.imprint","IMPRINT",EDGE,{"derivedFrom":sQuery(id+"F0.wireOp",EDGE,"E306")}),-1.0]])]});
            var Q20;
            Q20=makeQuery(id+"F0.imprint","IMPRINT",FACE,{"disambiguationData":[TD([[makeQuery(id+"F0.imprint","IMPRINT",EDGE,{"derivedFrom":sQuery(id+"F0.wireOp",EDGE,"E60.right")}),1.0]])]});
            var Q21;
            Q21=makeQuery(id+"F0.imprint","IMPRINT",FACE,{"disambiguationData":[TD([[makeQuery(id+"F0.imprint","IMPRINT",EDGE,{"derivedFrom":sQuery(id+"F0.wireOp",EDGE,"E229")}),-1.0]])]});
            var Q22;
            Q22=makeQuery(id+"F0.imprint","IMPRINT",FACE,{"disambiguationData":[TD([[makeQuery(id+"F0.imprint","IMPRINT",EDGE,{"derivedFrom":sQuery(id+"F0.wireOp",EDGE,"E314")}),-1.0]])]});
            var Q23;
            Q23=makeQuery(id+"F0.imprint","IMPRINT",FACE,{"disambiguationData":[TD([[makeQuery(id+"F0.imprint","IMPRINT",EDGE,{"derivedFrom":sQuery(id+"F0.wireOp",EDGE,"E62.top")}),1.0]])]});
            var Q24;
            Q24=makeQuery(id+"F0.imprint","IMPRINT",FACE,{"disambiguationData":[TD([[makeQuery(id+"F0.imprint","IMPRINT",EDGE,{"derivedFrom":sQuery(id+"F0.wireOp",EDGE,"E318")}),-1.0]])]});
            var Q25;
            Q25=makeQuery(id+"F0.imprint","IMPRINT",FACE,{"disambiguationData":[TD([[makeQuery(id+"F0.imprint","IMPRINT",EDGE,{"derivedFrom":sQuery(id+"F0.wireOp",EDGE,"E116")}),1.0]])]});
            var Q26;
            {var subQ1=sQuery(id+"F0.wireOp",EDGE,"E29.bottom");Q26=makeQuery(id+"F0.imprint","IMPRINT",FACE,{"disambiguationData":[TD([[makeQuery(id+"F0.imprint","IMPRINT",EDGE,{"derivedFrom":subQ1}),-1.0]])]});}
            var Q27;
            {var subQ2=sQuery(id+"F0.wireOp",EDGE,"E291");Q27=makeQuery(id+"F0.imprint","IMPRINT",FACE,{"disambiguationData":[TD([[makeQuery(id+"F0.imprint","IMPRINT",EDGE,{"derivedFrom":subQ2}),1.0]])]});}
            var Q28;
            Q28=makeQuery(id+"F0.imprint","IMPRINT",FACE,{"disambiguationData":[TD([[makeQuery(id+"F0.imprint","IMPRINT",EDGE,{"derivedFrom":sQuery(id+"F0.wireOp",EDGE,"E237")}),-1.0]])]});
            var Q29;
            {var subQ3=sQuery(id+"F0.wireOp",EDGE,"E13.bottom");Q29=makeQuery(id+"F0.imprint","IMPRINT",FACE,{"disambiguationData":[TD([[makeQuery(id+"F0.imprint","IMPRINT",EDGE,{"derivedFrom":subQ3}),-1.0]])]});}
            var Q30;
            Q30=makeQuery(id+"F0.imprint","IMPRINT",FACE,{"disambiguationData":[TD([[makeQuery(id+"F0.imprint","IMPRINT",EDGE,{"derivedFrom":sQuery(id+"F0.wireOp",EDGE,"E241")}),-1.0]])]});
            var Q31;
            Q31=makeQuery(id+"F0.imprint","IMPRINT",FACE,{"disambiguationData":[TD([[makeQuery(id+"F0.imprint","IMPRINT",EDGE,{"derivedFrom":sQuery(id+"F0.wireOp",EDGE,"E326")}),-1.0]])]});
            var Q32;
            Q32=makeQuery(id+"F0.imprint","IMPRINT",FACE,{"disambiguationData":[TD([[makeQuery(id+"F0.imprint","IMPRINT",EDGE,{"derivedFrom":sQuery(id+"F0.wireOp",EDGE,"E14.bottom")}),-1.0]])]});
            var Q33;
            Q33=makeQuery(id+"F0.imprint","IMPRINT",FACE,{"disambiguationData":[TD([[makeQuery(id+"F0.imprint","IMPRINT",EDGE,{"derivedFrom":sQuery(id+"F0.wireOp",EDGE,"E245")}),1.0]])]});
            var Q34;
            Q34=makeQuery(id+"F0.imprint","IMPRINT",FACE,{"disambiguationData":[TD([[makeQuery(id+"F0.imprint","IMPRINT",EDGE,{"derivedFrom":sQuery(id+"F0.wireOp",EDGE,"E138")}),1.0]])]});
            var Q35;
            Q35=makeQuery(id+"F0.imprint","IMPRINT",FACE,{"disambiguationData":[TD([[makeQuery(id+"F0.imprint","IMPRINT",EDGE,{"derivedFrom":sQuery(id+"F0.wireOp",EDGE,"E249")}),1.0]])]});
            var Q36;
            Q36=makeQuery(id+"F0.imprint","IMPRINT",FACE,{"disambiguationData":[TD([[makeQuery(id+"F0.imprint","IMPRINT",EDGE,{"derivedFrom":sQuery(id+"F0.wireOp",EDGE,"E253")}),-1.0]])]});
            var Q37;
            Q37=makeQuery(id+"F0.imprint","IMPRINT",FACE,{"disambiguationData":[TD([[makeQuery(id+"F0.imprint","IMPRINT",EDGE,{"derivedFrom":sQuery(id+"F0.wireOp",EDGE,"E257")}),-1.0]])]});
            var Q38;
            Q38=makeQuery(id+"F0.imprint","IMPRINT",FACE,{"disambiguationData":[TD([[makeQuery(id+"F0.imprint","IMPRINT",EDGE,{"derivedFrom":sQuery(id+"F0.wireOp",EDGE,"E171")}),1.0]])]});
            var Q39;
            Q39=makeQuery(id+"F0.imprint","IMPRINT",FACE,{"disambiguationData":[TD([[makeQuery(id+"F0.imprint","IMPRINT",EDGE,{"derivedFrom":sQuery(id+"F0.wireOp",EDGE,"E187")}),-1.0]])]});
            var Q40;
            {var subQ3=sQuery(id+"F0.wireOp",EDGE,"E21.bottom");Q40=makeQuery(id+"F0.imprint","IMPRINT",FACE,{"disambiguationData":[TD([[makeQuery(id+"F0.imprint","IMPRINT",EDGE,{"derivedFrom":subQ3}),-1.0]])]});}
            var Q41;
            Q41=makeQuery(id+"F0.imprint","IMPRINT",FACE,{"disambiguationData":[TD([[makeQuery(id+"F0.imprint","IMPRINT",EDGE,{"derivedFrom":sQuery(id+"F0.wireOp",EDGE,"E287")}),1.0]])]});
            var Q42;
            {var subQ3=sQuery(id+"F0.wireOp",EDGE,"E7.bottom");Q42=makeQuery(id+"F0.imprint","IMPRINT",FACE,{"disambiguationData":[TD([[makeQuery(id+"F0.imprint","IMPRINT",EDGE,{"derivedFrom":subQ3}),-1.0]])]});}
            var Q43;
            {var subQ3=sQuery(id+"F0.wireOp",EDGE,"E5.bottom");Q43=makeQuery(id+"F0.imprint","IMPRINT",FACE,{"disambiguationData":[TD([[makeQuery(id+"F0.imprint","IMPRINT",EDGE,{"derivedFrom":subQ3}),-1.0]])]});}
            var Q44;
            Q44=makeQuery(id+"F0.imprint","IMPRINT",FACE,{"disambiguationData":[TD([[makeQuery(id+"F0.imprint","IMPRINT",EDGE,{"derivedFrom":sQuery(id+"F0.wireOp",EDGE,"E10.top")}),1.0]])]});
            var Q45;
            {var subQ3=sQuery(id+"F0.wireOp",EDGE,"E64.bottom");Q45=makeQuery(id+"F0.imprint","IMPRINT",FACE,{"disambiguationData":[TD([[makeQuery(id+"F0.imprint","IMPRINT",EDGE,{"derivedFrom":subQ3}),-1.0]])]});}
            var Q46;
            Q46=makeQuery(id+"F0.imprint","IMPRINT",FACE,{"disambiguationData":[TD([[makeQuery(id+"F0.imprint","IMPRINT",EDGE,{"derivedFrom":sQuery(id+"F0.wireOp",EDGE,"E351")}),1.0]])]});
            var Q47;
            {var subQ3=sQuery(id+"F0.wireOp",EDGE,"E42.bottom");Q47=makeQuery(id+"F0.imprint","IMPRINT",FACE,{"disambiguationData":[TD([[makeQuery(id+"F0.imprint","IMPRINT",EDGE,{"derivedFrom":subQ3}),-1.0]])]});}
            var Q48;
            Q48=makeQuery(id+"F0.imprint","IMPRINT",FACE,{"disambiguationData":[TD([[makeQuery(id+"F0.imprint","IMPRINT",EDGE,{"derivedFrom":sQuery(id+"F0.wireOp",EDGE,"E22.top")}),1.0]])]});
            var Q49;
            Q49=makeQuery(id+"F0.imprint","IMPRINT",FACE,{"disambiguationData":[TD([[makeQuery(id+"F0.imprint","IMPRINT",EDGE,{"derivedFrom":sQuery(id+"F0.wireOp",EDGE,"E182")}),-1.0]])]});
            var Q50;
            Q50=makeQuery(id+"F0.imprint","IMPRINT",FACE,{"disambiguationData":[TD([[makeQuery(id+"F0.imprint","IMPRINT",EDGE,{"derivedFrom":sQuery(id+"F0.wireOp",EDGE,"E191")}),1.0]])]});
            var Q51;
            Q51=makeQuery(id+"F0.imprint","IMPRINT",FACE,{"disambiguationData":[TD([[makeQuery(id+"F0.imprint","IMPRINT",EDGE,{"derivedFrom":sQuery(id+"F0.wireOp",EDGE,"E298")}),-1.0]])]});
            var Q52;
            {var subQ0=sQuery(id+"F0.wireOp",EDGE,"E206");Q52=makeQuery(id+"F0.imprint","IMPRINT",FACE,{"disambiguationData":[TD([[makeQuery(id+"F0.imprint","IMPRINT",EDGE,{"derivedFrom":subQ0}),1.0]])]});}
            var Q53;
            Q53=makeQuery(id+"F0.imprint","IMPRINT",FACE,{"disambiguationData":[TD([[makeQuery(id+"F0.imprint","IMPRINT",EDGE,{"derivedFrom":sQuery(id+"F0.wireOp",EDGE,"E25.bottom")}),-1.0]])]});
            var Q54;
            Q54=makeQuery(id+"F0.imprint","IMPRINT",FACE,{"disambiguationData":[TD([[makeQuery(id+"F0.imprint","IMPRINT",EDGE,{"derivedFrom":sQuery(id+"F0.wireOp",EDGE,"E209")}),-1.0]])]});
            var Q55;
            {var subQ1=sQuery(id+"F0.wireOp",EDGE,"E8.bottom");Q55=makeQuery(id+"F0.imprint","IMPRINT",FACE,{"disambiguationData":[TD([[makeQuery(id+"F0.imprint","IMPRINT",EDGE,{"derivedFrom":subQ1}),-1.0]])]});}
            var Q56;
            {var subQ3=sQuery(id+"F0.wireOp",EDGE,"E26.bottom");Q56=makeQuery(id+"F0.imprint","IMPRINT",FACE,{"disambiguationData":[TD([[makeQuery(id+"F0.imprint","IMPRINT",EDGE,{"derivedFrom":subQ3}),-1.0]])]});}
            var Q57;
            Q57=makeQuery(id+"F0.imprint","IMPRINT",FACE,{"disambiguationData":[TD([[makeQuery(id+"F0.imprint","IMPRINT",EDGE,{"derivedFrom":sQuery(id+"F0.wireOp",EDGE,"E45.bottom")}),-1.0]])]});
            var Q58;
            {var subQ1=sQuery(id+"F0.wireOp",EDGE,"E27.bottom");Q58=makeQuery(id+"F0.imprint","IMPRINT",FACE,{"disambiguationData":[TD([[makeQuery(id+"F0.imprint","IMPRINT",EDGE,{"derivedFrom":subQ1}),-1.0]])]});}
            var Q59;
            Q59=makeQuery(id+"F0.imprint","IMPRINT",FACE,{"disambiguationData":[TD([[makeQuery(id+"F0.imprint","IMPRINT",EDGE,{"derivedFrom":sQuery(id+"F0.wireOp",EDGE,"E46.top")}),1.0]])]});
            var Q60;
            {var subQ3=sQuery(id+"F0.wireOp",EDGE,"E11.bottom");Q60=makeQuery(id+"F0.imprint","IMPRINT",FACE,{"disambiguationData":[TD([[makeQuery(id+"F0.imprint","IMPRINT",EDGE,{"derivedFrom":subQ3}),-1.0]])]});}
            var Q61;
            {var subQ3=sQuery(id+"F0.wireOp",EDGE,"E28.bottom");Q61=makeQuery(id+"F0.imprint","IMPRINT",FACE,{"disambiguationData":[TD([[makeQuery(id+"F0.imprint","IMPRINT",EDGE,{"derivedFrom":subQ3}),-1.0]])]});}
            var Q62;
            Q62=makeQuery(id+"F0.imprint","IMPRINT",FACE,{"disambiguationData":[TD([[makeQuery(id+"F0.imprint","IMPRINT",EDGE,{"derivedFrom":sQuery(id+"F0.wireOp",EDGE,"E47.bottom")}),-1.0]])]});
            var Q63;
            Q63=makeQuery(id+"F0.imprint","IMPRINT",FACE,{"disambiguationData":[TD([[makeQuery(id+"F0.imprint","IMPRINT",EDGE,{"derivedFrom":sQuery(id+"F0.wireOp",EDGE,"E233")}),-1.0]])]});
            var Q64;
            Q64=makeQuery(id+"F0.imprint","IMPRINT",FACE,{"disambiguationData":[TD([[makeQuery(id+"F0.imprint","IMPRINT",EDGE,{"derivedFrom":sQuery(id+"F0.wireOp",EDGE,"E48.top")}),1.0]])]});
            var Q65;
            Q65=makeQuery(id+"F0.imprint","IMPRINT",FACE,{"disambiguationData":[TD([[makeQuery(id+"F0.imprint","IMPRINT",EDGE,{"derivedFrom":sQuery(id+"F0.wireOp",EDGE,"E322")}),1.0]])]});
            var Q66;
            Q66=makeQuery(id+"F0.imprint","IMPRINT",FACE,{"disambiguationData":[TD([[makeQuery(id+"F0.imprint","IMPRINT",EDGE,{"derivedFrom":sQuery(id+"F0.wireOp",EDGE,"E124")}),-1.0]])]});
            var Q67;
            {var subQ3=sQuery(id+"F0.wireOp",EDGE,"E30.bottom");Q67=makeQuery(id+"F0.imprint","IMPRINT",FACE,{"disambiguationData":[TD([[makeQuery(id+"F0.imprint","IMPRINT",EDGE,{"derivedFrom":subQ3}),-1.0]])]});}
            var Q68;
            Q68=makeQuery(id+"F0.imprint","IMPRINT",FACE,{"disambiguationData":[TD([[makeQuery(id+"F0.imprint","IMPRINT",EDGE,{"derivedFrom":sQuery(id+"F0.wireOp",EDGE,"E49.bottom")}),-1.0]])]});
            var Q69;
            {var subQ1=sQuery(id+"F0.wireOp",EDGE,"E31.bottom");Q69=makeQuery(id+"F0.imprint","IMPRINT",FACE,{"disambiguationData":[TD([[makeQuery(id+"F0.imprint","IMPRINT",EDGE,{"derivedFrom":subQ1}),-1.0]])]});}
            var Q70;
            Q70=makeQuery(id+"F0.imprint","IMPRINT",FACE,{"disambiguationData":[TD([[makeQuery(id+"F0.imprint","IMPRINT",EDGE,{"derivedFrom":sQuery(id+"F0.wireOp",EDGE,"E330")}),-1.0]])]});
            var Q71;
            {var subQ3=sQuery(id+"F0.wireOp",EDGE,"E67.bottom");Q71=makeQuery(id+"F0.imprint","IMPRINT",FACE,{"disambiguationData":[TD([[makeQuery(id+"F0.imprint","IMPRINT",EDGE,{"derivedFrom":subQ3}),-1.0]])]});}
            var Q72;
            {var subQ3=sQuery(id+"F0.wireOp",EDGE,"E32.bottom");Q72=makeQuery(id+"F0.imprint","IMPRINT",FACE,{"disambiguationData":[TD([[makeQuery(id+"F0.imprint","IMPRINT",EDGE,{"derivedFrom":subQ3}),-1.0]])]});}
            var Q73;
            {var subQ1=sQuery(id+"F0.wireOp",EDGE,"E33.bottom");Q73=makeQuery(id+"F0.imprint","IMPRINT",FACE,{"disambiguationData":[TD([[makeQuery(id+"F0.imprint","IMPRINT",EDGE,{"derivedFrom":subQ1}),-1.0]])]});}
            var Q74;
            {var subQ3=sQuery(id+"F0.wireOp",EDGE,"E34.bottom");Q74=makeQuery(id+"F0.imprint","IMPRINT",FACE,{"disambiguationData":[TD([[makeQuery(id+"F0.imprint","IMPRINT",EDGE,{"derivedFrom":subQ3}),-1.0]])]});}
            var Q75;
            Q75=makeQuery(id+"F0.imprint","IMPRINT",FACE,{"disambiguationData":[TD([[makeQuery(id+"F0.imprint","IMPRINT",EDGE,{"derivedFrom":sQuery(id+"F0.wireOp",EDGE,"E261")}),-1.0]])]});
            var Q76;
            Q76=makeQuery(id+"F0.imprint","IMPRINT",FACE,{"disambiguationData":[TD([[makeQuery(id+"F0.imprint","IMPRINT",EDGE,{"derivedFrom":sQuery(id+"F0.wireOp",EDGE,"E183")}),-1.0]])]});
            var Q77;
            Q77=makeQuery(id+"F0.imprint","IMPRINT",FACE,{"disambiguationData":[TD([[makeQuery(id+"F0.imprint","IMPRINT",EDGE,{"derivedFrom":sQuery(id+"F0.wireOp",EDGE,"E20.top")}),1.0]])]});
            var Q78;
            {var subQ1=sQuery(id+"F0.wireOp",EDGE,"E35.bottom");Q78=makeQuery(id+"F0.imprint","IMPRINT",FACE,{"disambiguationData":[TD([[makeQuery(id+"F0.imprint","IMPRINT",EDGE,{"derivedFrom":subQ1}),-1.0]])]});}
            var Q79;
            Q79=makeQuery(id+"F0.imprint","IMPRINT",FACE,{"disambiguationData":[TD([[makeQuery(id+"F0.imprint","IMPRINT",EDGE,{"derivedFrom":sQuery(id+"F0.wireOp",EDGE,"E37.bottom")}),-1.0]])]});
            var Q80;
            {var subQ1=sQuery(id+"F0.wireOp",EDGE,"E6.bottom");Q80=makeQuery(id+"F0.imprint","IMPRINT",FACE,{"disambiguationData":[TD([[makeQuery(id+"F0.imprint","IMPRINT",EDGE,{"derivedFrom":subQ1}),-1.0]])]});}
            var Q81;
            Q81=makeQuery(id+"F0.imprint","IMPRINT",FACE,{"disambiguationData":[TD([[makeQuery(id+"F0.imprint","IMPRINT",EDGE,{"derivedFrom":sQuery(id+"F0.wireOp",EDGE,"E92")}),-1.0]])]});
            var Q82;
            Q82=makeQuery(id+"F0.imprint","IMPRINT",FACE,{"disambiguationData":[TD([[makeQuery(id+"F0.imprint","IMPRINT",EDGE,{"derivedFrom":sQuery(id+"F0.wireOp",EDGE,"E24.bottom")}),-1.0]])]});
            var Q83;
            {var subQ1=sQuery(id+"F0.wireOp",EDGE,"E50.top");Q83=makeQuery(id+"F0.imprint","IMPRINT",FACE,{"disambiguationData":[TD([[makeQuery(id+"F0.imprint","IMPRINT",EDGE,{"derivedFrom":subQ1}),1.0]])]});}
            var Q84;
            {var subQ1=sQuery(id+"F0.wireOp",EDGE,"E23.bottom");Q84=makeQuery(id+"F0.imprint","IMPRINT",FACE,{"disambiguationData":[TD([[makeQuery(id+"F0.imprint","IMPRINT",EDGE,{"derivedFrom":subQ1}),-1.0]])]});}
            var Q85;
            {var subQ3=sQuery(id+"F0.wireOp",EDGE,"E41.bottom");Q85=makeQuery(id+"F0.imprint","IMPRINT",FACE,{"disambiguationData":[TD([[makeQuery(id+"F0.imprint","IMPRINT",EDGE,{"derivedFrom":subQ3}),-1.0]])]});}
            var Q86;
            Q86=makeQuery(id+"F0.imprint","IMPRINT",FACE,{"disambiguationData":[TD([[makeQuery(id+"F0.imprint","IMPRINT",EDGE,{"derivedFrom":sQuery(id+"F0.wireOp",EDGE,"E310")}),-1.0]])]});
            var Q87;
            {var subQ3=sQuery(id+"F0.wireOp",EDGE,"E9.bottom");Q87=makeQuery(id+"F0.imprint","IMPRINT",FACE,{"disambiguationData":[TD([[makeQuery(id+"F0.imprint","IMPRINT",EDGE,{"derivedFrom":subQ3}),-1.0]])]});}
            var Q88;
            {var subQ1=sQuery(id+"F0.wireOp",EDGE,"E65.bottom");Q88=makeQuery(id+"F0.imprint","IMPRINT",FACE,{"disambiguationData":[TD([[makeQuery(id+"F0.imprint","IMPRINT",EDGE,{"derivedFrom":subQ1}),-1.0]])]});}
            var Q89;
            Q89=makeQuery(id+"F0.imprint","IMPRINT",FACE,{"disambiguationData":[TD([[makeQuery(id+"F0.imprint","IMPRINT",EDGE,{"derivedFrom":sQuery(id+"F0.wireOp",EDGE,"E51.bottom")}),-1.0]])]});
            var Q90;
            {var subQ1=sQuery(id+"F0.wireOp",EDGE,"E66.bottom");Q90=makeQuery(id+"F0.imprint","IMPRINT",FACE,{"disambiguationData":[TD([[makeQuery(id+"F0.imprint","IMPRINT",EDGE,{"derivedFrom":subQ1}),-1.0]])]});}
            var Q91;
            Q91=makeQuery(id+"F0.imprint","IMPRINT",FACE,{"disambiguationData":[TD([[makeQuery(id+"F0.imprint","IMPRINT",EDGE,{"derivedFrom":sQuery(id+"F0.wireOp",EDGE,"E52.top")}),1.0]])]});
            var Q92;
            Q92=makeQuery(id+"F0.imprint","IMPRINT",FACE,{"disambiguationData":[TD([[makeQuery(id+"F0.imprint","IMPRINT",EDGE,{"derivedFrom":sQuery(id+"F0.wireOp",EDGE,"E334")}),-1.0]])]});
            var Q93;
            Q93=makeQuery(id+"F0.imprint","IMPRINT",FACE,{"disambiguationData":[TD([[makeQuery(id+"F0.imprint","IMPRINT",EDGE,{"derivedFrom":sQuery(id+"F0.wireOp",EDGE,"E54.top")}),1.0]])]});
            var Q94;
            Q94=makeQuery(id+"F0.imprint","IMPRINT",FACE,{"disambiguationData":[TD([[makeQuery(id+"F0.imprint","IMPRINT",EDGE,{"derivedFrom":sQuery(id+"F0.wireOp",EDGE,"E163")}),1.0]])]});
            var Q95;
            Q95=makeQuery(id+"F0.imprint","IMPRINT",FACE,{"disambiguationData":[TD([[makeQuery(id+"F0.imprint","IMPRINT",EDGE,{"derivedFrom":sQuery(id+"F0.wireOp",EDGE,"E114")}),-1.0]])]});
            var Q96;
            Q96=makeQuery(id+"F0.imprint","IMPRINT",FACE,{"disambiguationData":[TD([[makeQuery(id+"F0.imprint","IMPRINT",EDGE,{"derivedFrom":sQuery(id+"F0.wireOp",EDGE,"E181")}),1.0]])]});
            var Q97;
            Q97=makeQuery(id+"F0.imprint","IMPRINT",FACE,{"disambiguationData":[TD([[makeQuery(id+"F0.imprint","IMPRINT",EDGE,{"derivedFrom":sQuery(id+"F0.wireOp",EDGE,"E195")}),-1.0]])]});
            var Q98;
            {var subQ3=sQuery(id+"F0.wireOp",EDGE,"E63.bottom");Q98=makeQuery(id+"F0.imprint","IMPRINT",FACE,{"disambiguationData":[TD([[makeQuery(id+"F0.imprint","IMPRINT",EDGE,{"derivedFrom":subQ3}),-1.0]])]});}
            var Q99;
            Q99=makeQuery(id+"F0.imprint","IMPRINT",FACE,{"disambiguationData":[TD([[makeQuery(id+"F0.imprint","IMPRINT",EDGE,{"derivedFrom":sQuery(id+"F0.wireOp",EDGE,"E58.left")}),-1.0]])]});
            var Q100;
            {var subQ1=sQuery(id+"F0.wireOp",EDGE,"E53.bottom");Q100=makeQuery(id+"F0.imprint","IMPRINT",FACE,{"disambiguationData":[TD([[makeQuery(id+"F0.imprint","IMPRINT",EDGE,{"derivedFrom":subQ1}),-1.0]])]});}
            var Q101;
            Q101=makeQuery(id+"F0.imprint","IMPRINT",FACE,{"disambiguationData":[TD([[makeQuery(id+"F0.imprint","IMPRINT",EDGE,{"derivedFrom":sQuery(id+"F0.wireOp",EDGE,"E225")}),-1.0]])]});
            var Q102;
            Q102=makeQuery(id+"F0.imprint","IMPRINT",FACE,{"disambiguationData":[TD([[makeQuery(id+"F0.imprint","IMPRINT",EDGE,{"derivedFrom":sQuery(id+"F0.wireOp",EDGE,"E97")}),-1.0]])]});
            var Q103;
            {var subQ0=sQuery(id+"F0.wireOp",EDGE,"E221");Q103=makeQuery(id+"F0.imprint","IMPRINT",FACE,{"disambiguationData":[TD([[makeQuery(id+"F0.imprint","IMPRINT",EDGE,{"derivedFrom":subQ0}),1.0]])]});}
            var Q104;
            Q104=makeQuery(id+"F0.imprint","IMPRINT",FACE,{"disambiguationData":[TD([[makeQuery(id+"F0.imprint","IMPRINT",EDGE,{"derivedFrom":sQuery(id+"F0.wireOp",EDGE,"E15.top")}),1.0]])]});
            var Q105;
            {var subQ0=sQuery(id+"F0.wireOp",EDGE,"E113");Q105=makeQuery(id+"F0.imprint","IMPRINT",FACE,{"disambiguationData":[TD([[makeQuery(id+"F0.imprint","IMPRINT",EDGE,{"derivedFrom":subQ0}),-1.0]])]});}
            var Q106;
            Q106=makeQuery(id+"F0.imprint","IMPRINT",FACE,{"disambiguationData":[TD([[makeQuery(id+"F0.imprint","IMPRINT",EDGE,{"derivedFrom":sQuery(id+"F0.wireOp",EDGE,"E338")}),-1.0]])]});
            var Q107;
            {var subQ1=sQuery(id+"F0.wireOp",EDGE,"E55.bottom");Q107=makeQuery(id+"F0.imprint","IMPRINT",FACE,{"disambiguationData":[TD([[makeQuery(id+"F0.imprint","IMPRINT",EDGE,{"derivedFrom":subQ1}),-1.0]])]});}
            var Q108;
            Q108=makeQuery(id+"F0.imprint","IMPRINT",FACE,{"disambiguationData":[TD([[makeQuery(id+"F0.imprint","IMPRINT",EDGE,{"derivedFrom":sQuery(id+"F0.wireOp",EDGE,"E91")}),1.0]])]});
            var Q109;
            {var subQ0=sQuery(id+"F0.wireOp",EDGE,"E12.left");Q109=makeQuery(id+"F0.imprint","IMPRINT",FACE,{"disambiguationData":[TD([[makeQuery(id+"F0.imprint","IMPRINT",EDGE,{"derivedFrom":subQ0}),1.0]])]});}
            var Q110;
            Q110=makeQuery(id+"F0.imprint","IMPRINT",FACE,{"disambiguationData":[TD([[makeQuery(id+"F0.imprint","IMPRINT",EDGE,{"derivedFrom":sQuery(id+"F0.wireOp",EDGE,"E19.bottom")}),-1.0]])]});
            var Q111;
            {var subQ3=sQuery(id+"F0.wireOp",EDGE,"E36.bottom");Q111=makeQuery(id+"F0.imprint","IMPRINT",FACE,{"disambiguationData":[TD([[makeQuery(id+"F0.imprint","IMPRINT",EDGE,{"derivedFrom":subQ3}),-1.0]])]});}
            var Q112;
            Q112=makeQuery(id+"F0.imprint","IMPRINT",FACE,{"disambiguationData":[TD([[makeQuery(id+"F0.imprint","IMPRINT",EDGE,{"derivedFrom":sQuery(id+"F0.wireOp",EDGE,"E58.bottom")}),-1.0]])]});
            var Q113;
            Q113=makeQuery(id+"F0.imprint","IMPRINT",FACE,{"disambiguationData":[TD([[makeQuery(id+"F0.imprint","IMPRINT",EDGE,{"derivedFrom":sQuery(id+"F0.wireOp",EDGE,"E175")}),1.0]])]});
            var Q114;
            Q114=makeQuery(id+"F0.imprint","IMPRINT",FACE,{"disambiguationData":[TD([[makeQuery(id+"F0.imprint","IMPRINT",EDGE,{"derivedFrom":sQuery(id+"F0.wireOp",EDGE,"E57.left")}),-1.0]])]});
            var Q115;
            Q115=makeQuery(id+"F0.imprint","IMPRINT",FACE,{"disambiguationData":[TD([[makeQuery(id+"F0.imprint","IMPRINT",EDGE,{"derivedFrom":sQuery(id+"F0.wireOp",EDGE,"E59.top")}),1.0]])]});
            var Q116;
            Q116=makeQuery(id+"F0.imprint","IMPRINT",FACE,{"disambiguationData":[TD([[makeQuery(id+"F0.imprint","IMPRINT",EDGE,{"derivedFrom":sQuery(id+"F0.wireOp",EDGE,"E60.bottom")}),-1.0]])]});
            var Q117;
            Q117=makeQuery(id+"F0.imprint","IMPRINT",FACE,{"disambiguationData":[TD([[makeQuery(id+"F0.imprint","IMPRINT",EDGE,{"derivedFrom":sQuery(id+"F0.wireOp",EDGE,"E61.bottom")}),-1.0]])]});
            var Q118;
            Q118=makeQuery(id+"F0.imprint","IMPRINT",FACE,{"disambiguationData":[TD([[makeQuery(id+"F0.imprint","IMPRINT",EDGE,{"derivedFrom":sQuery(id+"F0.wireOp",EDGE,"E155")}),-1.0]])]});
            var Q119;
            Q119=makeQuery(id+"F0.imprint","IMPRINT",FACE,{"disambiguationData":[TD([[makeQuery(id+"F0.imprint","IMPRINT",EDGE,{"derivedFrom":sQuery(id+"F0.wireOp",EDGE,"E56.bottom")}),-1.0]])]});
            var Q120;
            Q120=makeQuery(id+"F0.imprint","IMPRINT",FACE,{"disambiguationData":[TD([[makeQuery(id+"F0.imprint","IMPRINT",EDGE,{"derivedFrom":sQuery(id+"F0.wireOp",EDGE,"E57.bottom")}),-1.0]])]});
            var Q121;
            Q121=makeQuery(id+"F0.imprint","IMPRINT",FACE,{"disambiguationData":[TD([[makeQuery(id+"F0.imprint","IMPRINT",EDGE,{"derivedFrom":sQuery(id+"F0.wireOp",EDGE,"E280")}),-1.0]])]});
            var Q122;
            Q122=makeQuery(id+"F0.imprint","IMPRINT",FACE,{"disambiguationData":[TD([[makeQuery(id+"F0.imprint","IMPRINT",EDGE,{"derivedFrom":sQuery(id+"F0.wireOp",EDGE,"E16.top")}),1.0]])]});
            var Q123;
            Q123=makeQuery(id+"F0.imprint","IMPRINT",FACE,{"disambiguationData":[TD([[makeQuery(id+"F0.imprint","IMPRINT",EDGE,{"derivedFrom":sQuery(id+"F0.wireOp",EDGE,"E18.bottom")}),-1.0]])]});
            var Q124;
            {var subQ1=sQuery(id+"F0.wireOp",EDGE,"E17.bottom");Q124=makeQuery(id+"F0.imprint","IMPRINT",FACE,{"disambiguationData":[TD([[makeQuery(id+"F0.imprint","IMPRINT",EDGE,{"derivedFrom":subQ1}),-1.0]])]});}
            var Q125;
            Q125=makeQuery(id+"F0.imprint","IMPRINT",FACE,{"disambiguationData":[TD([[makeQuery(id+"F0.imprint","IMPRINT",EDGE,{"derivedFrom":sQuery(id+"F0.wireOp",EDGE,"E109")}),-1.0]])]});
            var Q126;
            Q126=makeQuery(id+"F0.imprint","IMPRINT",FACE,{"disambiguationData":[TD([[makeQuery(id+"F0.imprint","IMPRINT",EDGE,{"derivedFrom":sQuery(id+"F0.wireOp",EDGE,"E102")}),1.0]])]});
            var Q127;
            Q127=makeQuery(id+"F0.imprint","IMPRINT",FACE,{"disambiguationData":[TD([[makeQuery(id+"F0.imprint","IMPRINT",EDGE,{"derivedFrom":sQuery(id+"F0.wireOp",EDGE,"E76")}),-1.0]])]});
            var Q128;
            Q128=makeQuery(id+"F0.imprint","IMPRINT",FACE,{"disambiguationData":[TD([[makeQuery(id+"F0.imprint","IMPRINT",EDGE,{"derivedFrom":sQuery(id+"F0.wireOp",EDGE,"E73")}),-1.0]])]});
            extrude(context, id + "F2", {"entities" : qUnion([Q0, Q1, Q2, Q3, Q4, Q5, Q6, Q7, Q8, Q9, Q10, Q11, Q12, Q13, Q14, Q15, Q16, Q17, Q18, Q19, Q20, Q21, Q22, Q23, Q24, Q25, Q26, Q27, Q28, Q29, Q30, Q31, Q32, Q33, Q34, Q35, Q36, Q37, Q38, Q39, Q40, Q41, Q42, Q43, Q44, Q45, Q46, Q47, Q48, Q49, Q50, Q51, Q52, Q53, Q54, Q55, Q56, Q57, Q58, Q59, Q60, Q61, Q62, Q63, Q64, Q65, Q66, Q67, Q68, Q69, Q70, Q71, Q72, Q73, Q74, Q75, Q76, Q77, Q78, Q79, Q80, Q81, Q82, Q83, Q84, Q85, Q86, Q87, Q88, Q89, Q90, Q91, Q92, Q93, Q94, Q95, Q96, Q97, Q98, Q99, Q100, Q101, Q102, Q103, Q104, Q105, Q106, Q107, Q108, Q109, Q110, Q111, Q112, Q113, Q114, Q115, Q116, Q117, Q118, Q119, Q120, Q121, Q122, Q123, Q124, Q125, Q126, Q127, Q128]), "depth" : 0.64 * mm, "offsetDistance" : 25.4 * mm});
        }
        {
            var Q0;
            Q0=makeQuery(id+"F1.imprint","IMPRINT",FACE,{"disambiguationData":[TD([[makeQuery(id+"F1.imprint","IMPRINT",EDGE,{"derivedFrom":sQuery(id+"F1.wireOp",EDGE,"E380")}),-1.0]])]});
            var Q1;
            Q1=makeQuery(id+"F1.imprint","IMPRINT",FACE,{"disambiguationData":[TD([[makeQuery(id+"F1.imprint","IMPRINT",EDGE,{"derivedFrom":sQuery(id+"F1.wireOp",EDGE,"E511.bottom")}),1.0]])]});
            var Q2;
            Q2=makeQuery(id+"F1.imprint","IMPRINT",FACE,{"disambiguationData":[TD([[makeQuery(id+"F1.imprint","IMPRINT",EDGE,{"derivedFrom":sQuery(id+"F1.wireOp",EDGE,"E504.bottom")}),1.0]])]});
            var Q3;
            Q3=makeQuery(id+"F1.imprint","IMPRINT",FACE,{"disambiguationData":[TD([[makeQuery(id+"F1.imprint","IMPRINT",EDGE,{"derivedFrom":sQuery(id+"F1.wireOp",EDGE,"E503.bottom")}),1.0]])]});
            var Q4;
            Q4=makeQuery(id+"F1.imprint","IMPRINT",FACE,{"disambiguationData":[TD([[makeQuery(id+"F1.imprint","IMPRINT",EDGE,{"derivedFrom":sQuery(id+"F1.wireOp",EDGE,"E502.bottom")}),1.0]])]});
            var Q5;
            Q5=makeQuery(id+"F1.imprint","IMPRINT",FACE,{"disambiguationData":[TD([[makeQuery(id+"F1.imprint","IMPRINT",EDGE,{"derivedFrom":sQuery(id+"F1.wireOp",EDGE,"E501.bottom")}),1.0]])]});
            var Q6;
            Q6=makeQuery(id+"F1.imprint","IMPRINT",FACE,{"disambiguationData":[TD([[makeQuery(id+"F1.imprint","IMPRINT",EDGE,{"derivedFrom":sQuery(id+"F1.wireOp",EDGE,"E500.bottom")}),1.0]])]});
            var Q7;
            Q7=makeQuery(id+"F1.imprint","IMPRINT",FACE,{"disambiguationData":[TD([[makeQuery(id+"F1.imprint","IMPRINT",EDGE,{"derivedFrom":sQuery(id+"F1.wireOp",EDGE,"E499.bottom")}),1.0]])]});
            var Q8;
            Q8=makeQuery(id+"F1.imprint","IMPRINT",FACE,{"disambiguationData":[TD([[makeQuery(id+"F1.imprint","IMPRINT",EDGE,{"derivedFrom":sQuery(id+"F1.wireOp",EDGE,"E498.bottom")}),1.0]])]});
            var Q9;
            Q9=makeQuery(id+"F1.imprint","IMPRINT",FACE,{"disambiguationData":[TD([[makeQuery(id+"F1.imprint","IMPRINT",EDGE,{"derivedFrom":sQuery(id+"F1.wireOp",EDGE,"E497.bottom")}),1.0]])]});
            var Q10;
            Q10=makeQuery(id+"F1.imprint","IMPRINT",FACE,{"disambiguationData":[TD([[makeQuery(id+"F1.imprint","IMPRINT",EDGE,{"derivedFrom":sQuery(id+"F1.wireOp",EDGE,"E496.bottom")}),1.0]])]});
            var Q11;
            Q11=makeQuery(id+"F1.imprint","IMPRINT",FACE,{"disambiguationData":[TD([[makeQuery(id+"F1.imprint","IMPRINT",EDGE,{"derivedFrom":sQuery(id+"F1.wireOp",EDGE,"E495.bottom")}),1.0]])]});
            var Q12;
            Q12=makeQuery(id+"F1.imprint","IMPRINT",FACE,{"disambiguationData":[TD([[makeQuery(id+"F1.imprint","IMPRINT",EDGE,{"derivedFrom":sQuery(id+"F1.wireOp",EDGE,"E494.bottom")}),1.0]])]});
            var Q13;
            Q13=makeQuery(id+"F1.imprint","IMPRINT",FACE,{"disambiguationData":[TD([[makeQuery(id+"F1.imprint","IMPRINT",EDGE,{"derivedFrom":sQuery(id+"F1.wireOp",EDGE,"E493.bottom")}),1.0]])]});
            var Q14;
            Q14=makeQuery(id+"F1.imprint","IMPRINT",FACE,{"disambiguationData":[TD([[makeQuery(id+"F1.imprint","IMPRINT",EDGE,{"derivedFrom":sQuery(id+"F1.wireOp",EDGE,"E491.bottom")}),1.0]])]});
            var Q15;
            Q15=makeQuery(id+"F1.imprint","IMPRINT",FACE,{"disambiguationData":[TD([[makeQuery(id+"F1.imprint","IMPRINT",EDGE,{"derivedFrom":sQuery(id+"F1.wireOp",EDGE,"E490.bottom")}),1.0]])]});
            var Q16;
            Q16=makeQuery(id+"F1.imprint","IMPRINT",FACE,{"disambiguationData":[TD([[makeQuery(id+"F1.imprint","IMPRINT",EDGE,{"derivedFrom":sQuery(id+"F1.wireOp",EDGE,"E505.bottom")}),1.0]])]});
            var Q17;
            Q17=makeQuery(id+"F1.imprint","IMPRINT",FACE,{"disambiguationData":[TD([[makeQuery(id+"F1.imprint","IMPRINT",EDGE,{"derivedFrom":sQuery(id+"F1.wireOp",EDGE,"E384")}),-1.0]])]});
            var Q18;
            Q18=makeQuery(id+"F1.imprint","IMPRINT",FACE,{"disambiguationData":[TD([[makeQuery(id+"F1.imprint","IMPRINT",EDGE,{"derivedFrom":sQuery(id+"F1.wireOp",EDGE,"E382")}),-1.0]])]});
            var Q19;
            Q19=makeQuery(id+"F1.imprint","IMPRINT",FACE,{"disambiguationData":[TD([[makeQuery(id+"F1.imprint","IMPRINT",EDGE,{"derivedFrom":sQuery(id+"F1.wireOp",EDGE,"E492.bottom")}),1.0]])]});
            var Q20;
            Q20=makeQuery(id+"F1.imprint","IMPRINT",FACE,{"disambiguationData":[TD([[makeQuery(id+"F1.imprint","IMPRINT",EDGE,{"derivedFrom":sQuery(id+"F1.wireOp",EDGE,"E592.top")}),1.0]])]});
            var Q21;
            Q21=makeQuery(id+"F1.imprint","IMPRINT",FACE,{"disambiguationData":[TD([[makeQuery(id+"F1.imprint","IMPRINT",EDGE,{"derivedFrom":sQuery(id+"F1.wireOp",EDGE,"E386.top")}),1.0]])]});
            var Q22;
            Q22=makeQuery(id+"F1.imprint","IMPRINT",FACE,{"disambiguationData":[TD([[makeQuery(id+"F1.imprint","IMPRINT",EDGE,{"derivedFrom":sQuery(id+"F1.wireOp",EDGE,"E374")}),-1.0]])]});
            var Q23;
            Q23=makeQuery(id+"F1.imprint","IMPRINT",FACE,{"disambiguationData":[TD([[makeQuery(id+"F1.imprint","IMPRINT",EDGE,{"derivedFrom":sQuery(id+"F1.wireOp",EDGE,"E376")}),-1.0]])]});
            var Q24;
            Q24=makeQuery(id+"F1.imprint","IMPRINT",FACE,{"disambiguationData":[TD([[makeQuery(id+"F1.imprint","IMPRINT",EDGE,{"derivedFrom":sQuery(id+"F1.wireOp",EDGE,"E378")}),-1.0]])]});
            var Q25;
            {var subQ1=sQuery(id+"F1.wireOp",EDGE,"E390.bottom");Q25=makeQuery(id+"F1.imprint","IMPRINT",FACE,{"disambiguationData":[TD([[makeQuery(id+"F1.imprint","IMPRINT",EDGE,{"derivedFrom":subQ1}),1.0]])]});}
            var Q26;
            Q26=makeQuery(id+"F1.imprint","IMPRINT",FACE,{"disambiguationData":[TD([[makeQuery(id+"F1.imprint","IMPRINT",EDGE,{"derivedFrom":sQuery(id+"F1.wireOp",EDGE,"E391.bottom")}),1.0]])]});
            var Q27;
            Q27=makeQuery(id+"F1.imprint","IMPRINT",FACE,{"disambiguationData":[TD([[makeQuery(id+"F1.imprint","IMPRINT",EDGE,{"derivedFrom":sQuery(id+"F1.wireOp",EDGE,"E393.bottom")}),1.0]])]});
            var Q28;
            Q28=makeQuery(id+"F1.imprint","IMPRINT",FACE,{"disambiguationData":[TD([[makeQuery(id+"F1.imprint","IMPRINT",EDGE,{"derivedFrom":sQuery(id+"F1.wireOp",EDGE,"E394.bottom")}),1.0]])]});
            var Q29;
            Q29=makeQuery(id+"F1.imprint","IMPRINT",FACE,{"disambiguationData":[TD([[makeQuery(id+"F1.imprint","IMPRINT",EDGE,{"derivedFrom":sQuery(id+"F1.wireOp",EDGE,"E395.bottom")}),1.0]])]});
            var Q30;
            Q30=makeQuery(id+"F1.imprint","IMPRINT",FACE,{"disambiguationData":[TD([[makeQuery(id+"F1.imprint","IMPRINT",EDGE,{"derivedFrom":sQuery(id+"F1.wireOp",EDGE,"E396.bottom")}),1.0]])]});
            var Q31;
            Q31=makeQuery(id+"F1.imprint","IMPRINT",FACE,{"disambiguationData":[TD([[makeQuery(id+"F1.imprint","IMPRINT",EDGE,{"derivedFrom":sQuery(id+"F1.wireOp",EDGE,"E397.bottom")}),1.0]])]});
            var Q32;
            Q32=makeQuery(id+"F1.imprint","IMPRINT",FACE,{"disambiguationData":[TD([[makeQuery(id+"F1.imprint","IMPRINT",EDGE,{"derivedFrom":sQuery(id+"F1.wireOp",EDGE,"E398.bottom")}),1.0]])]});
            var Q33;
            Q33=makeQuery(id+"F1.imprint","IMPRINT",FACE,{"disambiguationData":[TD([[makeQuery(id+"F1.imprint","IMPRINT",EDGE,{"derivedFrom":sQuery(id+"F1.wireOp",EDGE,"E434.bottom")}),1.0]])]});
            var Q34;
            Q34=makeQuery(id+"F1.imprint","IMPRINT",FACE,{"disambiguationData":[TD([[makeQuery(id+"F1.imprint","IMPRINT",EDGE,{"derivedFrom":sQuery(id+"F1.wireOp",EDGE,"E436.bottom")}),1.0]])]});
            var Q35;
            Q35=makeQuery(id+"F1.imprint","IMPRINT",FACE,{"disambiguationData":[TD([[makeQuery(id+"F1.imprint","IMPRINT",EDGE,{"derivedFrom":sQuery(id+"F1.wireOp",EDGE,"E437.bottom")}),1.0]])]});
            var Q36;
            Q36=makeQuery(id+"F1.imprint","IMPRINT",FACE,{"disambiguationData":[TD([[makeQuery(id+"F1.imprint","IMPRINT",EDGE,{"derivedFrom":sQuery(id+"F1.wireOp",EDGE,"E438.bottom")}),1.0]])]});
            var Q37;
            Q37=makeQuery(id+"F1.imprint","IMPRINT",FACE,{"disambiguationData":[TD([[makeQuery(id+"F1.imprint","IMPRINT",EDGE,{"derivedFrom":sQuery(id+"F1.wireOp",EDGE,"E439.bottom")}),1.0]])]});
            var Q38;
            Q38=makeQuery(id+"F1.imprint","IMPRINT",FACE,{"disambiguationData":[TD([[makeQuery(id+"F1.imprint","IMPRINT",EDGE,{"derivedFrom":sQuery(id+"F1.wireOp",EDGE,"E441.bottom")}),1.0]])]});
            var Q39;
            Q39=makeQuery(id+"F1.imprint","IMPRINT",FACE,{"disambiguationData":[TD([[makeQuery(id+"F1.imprint","IMPRINT",EDGE,{"derivedFrom":sQuery(id+"F1.wireOp",EDGE,"E442.bottom")}),1.0]])]});
            var Q40;
            Q40=makeQuery(id+"F1.imprint","IMPRINT",FACE,{"disambiguationData":[TD([[makeQuery(id+"F1.imprint","IMPRINT",EDGE,{"derivedFrom":sQuery(id+"F1.wireOp",EDGE,"E444.bottom")}),1.0]])]});
            var Q41;
            Q41=makeQuery(id+"F1.imprint","IMPRINT",FACE,{"disambiguationData":[TD([[makeQuery(id+"F1.imprint","IMPRINT",EDGE,{"derivedFrom":sQuery(id+"F1.wireOp",EDGE,"E440.bottom")}),1.0]])]});
            extrude(context, id + "F3", {"entities" : qUnion([Q0, Q1, Q2, Q3, Q4, Q5, Q6, Q7, Q8, Q9, Q10, Q11, Q12, Q13, Q14, Q15, Q16, Q17, Q18, Q19, Q20, Q21, Q22, Q23, Q24, Q25, Q26, Q27, Q28, Q29, Q30, Q31, Q32, Q33, Q34, Q35, Q36, Q37, Q38, Q39, Q40, Q41]), "depth" : 0.64 * mm, "offsetDistance" : 25.4 * mm});
        }
    });
